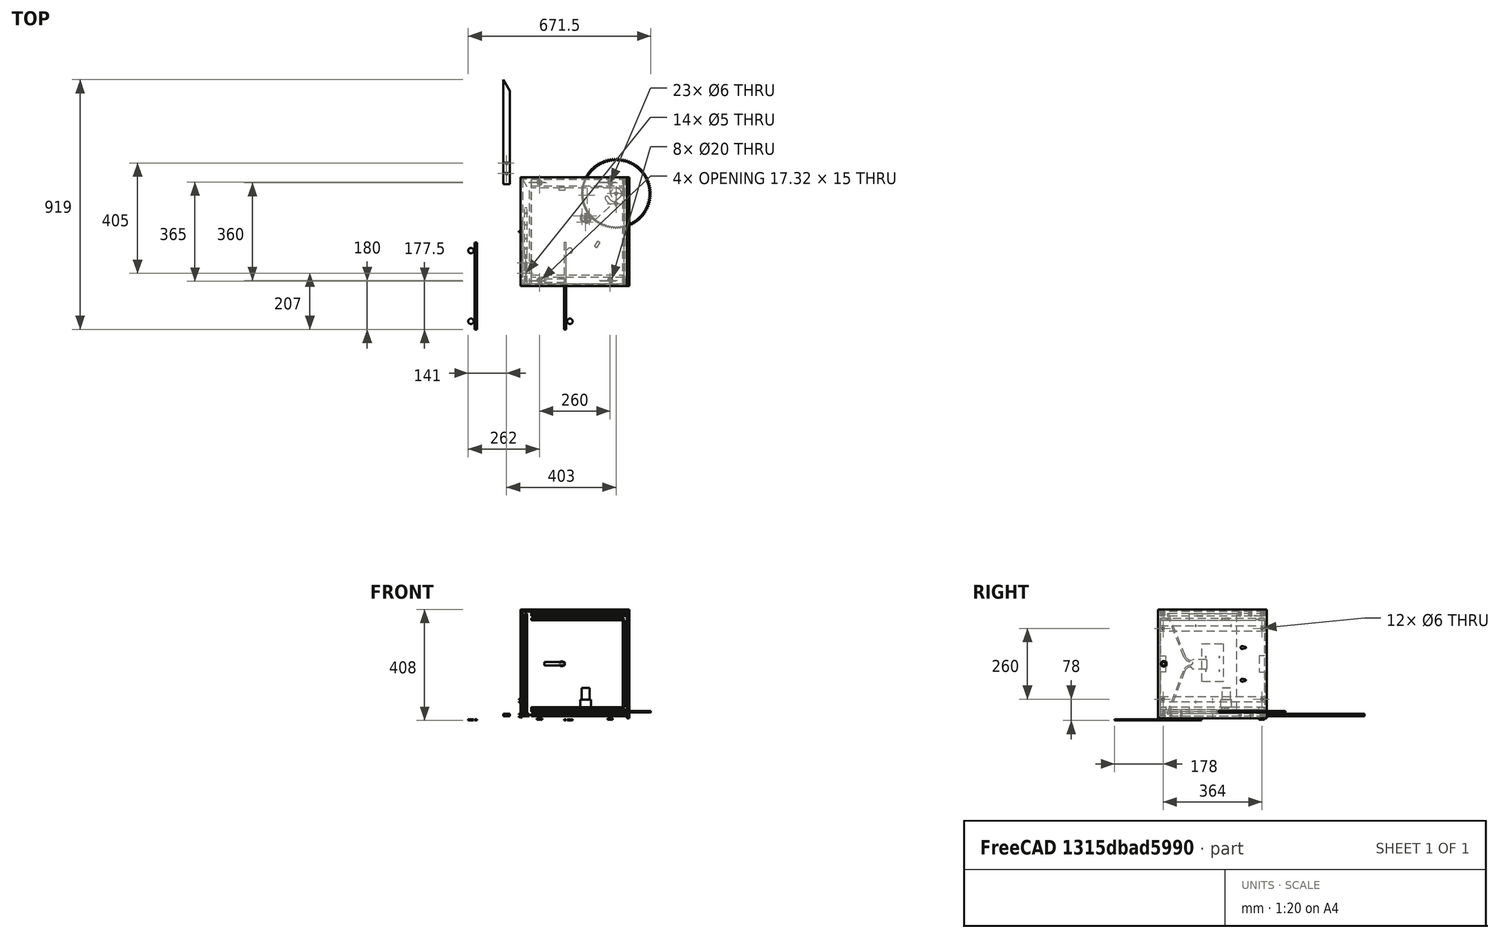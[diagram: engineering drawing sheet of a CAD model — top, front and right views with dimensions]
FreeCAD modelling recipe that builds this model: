
FCSTD DOCUMENT  (FreeCAD 0.16R6707 (Git))
Label: Latskap
License: All rights reserved
LicenseURL: http://en.wikipedia.org/wiki/All_rights_reserved
objects: Sketcher::SketchObject×47, Part::Part2DObjectPython×33, PartDesign::Pad×29, PartDesign::Pocket×18, Part::FeaturePython×9, Part::Feature×7, Part::Mirroring×6, PartDesign::Draft×5, App::DocumentObjectGroup×5, PartDesign::LinearPattern×2, Spreadsheet::Sheet×2, PartDesign::Revolution×1, PartDesign::Mirrored×1, PartDesign::MultiTransform×1, Mesh::Feature×1
note: 207 computed .brp shape members not serialized (recipe doc carries the construction recipe); baked Part::Feature solids carry a one-line shape summary decoded from their .brp

FEATURE [Sketcher::SketchObject] Sketch003
  expr: Constraints[8] = Latskap.width
  expr: Constraints[10] = Latskap.height
  sketch-geometry (4):
    g0: LineSegment StartX=0 StartY=-200 StartZ=0 EndX=400 EndY=-200 EndZ=0
    g1: LineSegment StartX=400 StartY=-200 StartZ=0 EndX=400 EndY=200 EndZ=0
    g2: LineSegment StartX=400 StartY=200 StartZ=0 EndX=0 EndY=200 EndZ=0
    g3: LineSegment StartX=0 StartY=200 StartZ=0 EndX=0 EndY=-200 EndZ=0
  constraints (12):
    c: Coincident(g0,g1)
    c: Coincident(g1,g2)
    c: Coincident(g2,g3)
    c: Coincident(g3,g0)
    c: Horizontal(g0)
    c: Horizontal(g2)
    c: Vertical(g1)
    c: Vertical(g3)
    c: DistanceX(g2,g2) = 400
    c: PointOnObject(g2,g-2)
    c: DistanceY(g1,g1) = 400
    c: Symmetric(g1,g0,g-1)
FEATURE [PartDesign::Pad] Pad002  label="Wall-outer"
  Length = 8
  Length2 = 100
  Sketch = -> Sketch003
  Type = 0
FEATURE [Sketcher::SketchObject] Sketch006
  Placement = pos=(0,0,8) rot=(0,0,1;0rad)
  expr: Constraints[36] = (Latskap.width - Latskap.bolt_distance) / 2
  expr: Constraints[11] = Latskap.arm_offset
  expr: Constraints[16] = Latskap.arm_offset
  expr: Constraints[35] = Latskap.bolt_offset
  expr: Constraints[32] = Latskap.bolt_distance
  expr: Constraints[6] = Latskap.wall_inner
  sketch-geometry (14):
    g0: LineSegment StartX=40 StartY=192 StartZ=0 EndX=392 EndY=192 EndZ=0
    g1: LineSegment StartX=392 StartY=192 StartZ=0 EndX=392 EndY=-192 EndZ=0
    g2: LineSegment StartX=392 StartY=-192 StartZ=0 EndX=40 EndY=-192 EndZ=0
    g3: LineSegment StartX=40 StartY=192 StartZ=0 EndX=40 EndY=-192 EndZ=0
    g4: Circle CenterX=352 CenterY=102 CenterZ=0 NormalX=0 NormalY=0 NormalZ=1 Radius=2.5
    g5: Circle CenterX=352 CenterY=140 CenterZ=0 NormalX=0 NormalY=0 NormalZ=1 Radius=2.5
    g6: Circle CenterX=70 CenterY=180 CenterZ=0 NormalX=0 NormalY=0 NormalZ=1 Radius=3
    g7: Circle CenterX=330 CenterY=180 CenterZ=0 NormalX=0 NormalY=0 NormalZ=1 Radius=3
    g8: Circle CenterX=70 CenterY=-179.546 CenterZ=0 NormalX=0 NormalY=0 NormalZ=1 Radius=3
    g9: Circle CenterX=330 CenterY=-179.546 CenterZ=0 NormalX=0 NormalY=0 NormalZ=1 Radius=3
    g10: LineSegment [constr] StartX=70 StartY=180 StartZ=0 EndX=330 EndY=180 EndZ=0
    g11: LineSegment [constr] StartX=330 StartY=180 StartZ=0 EndX=330 EndY=-179.546 EndZ=0
    g12: LineSegment [constr] StartX=330 StartY=-179.546 StartZ=0 EndX=70 EndY=-179.546 EndZ=0
    g13: LineSegment [constr] StartX=70 StartY=-179.546 StartZ=0 EndX=70 EndY=180 EndZ=0
  constraints (37):
    c: Coincident(g0,g1)
    c: Coincident(g1,g2)
    c: Horizontal(g0)
    c: Horizontal(g2)
    c: Vertical(g1)
    c: DistanceX(g0,g0) = 352
    c: DistanceY(g1,g1) = 384
    c: Symmetric(g0,g2,g-1)
    c: Vertical(g3)
    c: Coincident(g2,g3)
    c: Radius(g4) = 2.5
    c: DistanceX(g4) = 352
    c: DistanceY(g4) = 102
    c: DistanceX(g0) = 40
    c: Coincident(g0,g3)
    c: Radius(g5) = 2.5
    c: DistanceX(g5) = 352
    c: DistanceY(g4,g5) = 38
    c: Equal(g6,g7)
    c: Equal(g7,g8)
    c: Equal(g8,g9)
    c: Radius(g9) = 3
    c: Coincident(g10,g11)
    c: Coincident(g11,g12)
    c: Coincident(g12,g13)
    c: Coincident(g13,g10)
    c: Horizontal(g10)
    c: Horizontal(g12)
    c: Vertical(g11)
    c: Vertical(g13)
    c: Coincident(g9,g11)
    c: Coincident(g8,g12)
    c: DistanceX(g12,g12) = 260
    c: Coincident(g10,g7)
    c: Coincident(g6,g10)
    c: DistanceY(g7) = 180
    c: DistanceX(g6) = 70
FEATURE [PartDesign::Pad] Pad004  label="Wall-1-1"
  Length = 8
  Length2 = 100
  Placement = pos=(0,0,8) rot=(0,0,1;0rad)
  Sketch = -> Sketch006
  Type = 0
FEATURE [Sketcher::SketchObject] Sketch012
  expr: Constraints[9] = Latskap.height
  sketch-geometry (4):
    g0: LineSegment StartX=8 StartY=-200 StartZ=0 EndX=0 EndY=-200 EndZ=0
    g1: LineSegment StartX=0 StartY=-200 StartZ=0 EndX=0 EndY=200 EndZ=0
    g2: LineSegment StartX=0 StartY=200 StartZ=0 EndX=8 EndY=200 EndZ=0
    g3: LineSegment StartX=8 StartY=200 StartZ=0 EndX=8 EndY=-200 EndZ=0
  constraints (12):
    c: Coincident(g0,g1)
    c: Coincident(g1,g2)
    c: Coincident(g2,g3)
    c: Coincident(g3,g0)
    c: Horizontal(g0)
    c: Horizontal(g2)
    c: Vertical(g1)
    c: Vertical(g3)
    c: DistanceX(g2,g2) = 8
    c: DistanceY(g1,g1) = 400
    c: Symmetric(g1,g0,g-1)
    c: DistanceX(g1) = 0
FEATURE [PartDesign::Pad] Pad008  label="Door-outer"
  Length = 400
  Length2 = 100
  Sketch = -> Sketch012
  Type = 0
FEATURE [Sketcher::SketchObject] Sketch014
  Placement = pos=(0,0,16) rot=(0,0,1;0rad)
  sketch-geometry (11):
    g0: LineSegment StartX=20 StartY=-163 StartZ=0 EndX=186.401 EndY=-163 EndZ=0
    g1: LineSegment StartX=194.788 StartY=-158.446 StartZ=0 EndX=360.387 EndY=96.5536 EndZ=0
    g2: LineSegment StartX=343.613 StartY=107.446 StartZ=0 EndX=183.929 EndY=-138.446 EndZ=0
    g3: LineSegment StartX=175.542 StartY=-143 StartZ=0 EndX=20 EndY=-143 EndZ=0
    g4: ArcOfCircle CenterX=20 CenterY=-153 CenterZ=0 NormalX=0 NormalY=0 NormalZ=1 Radius=10 StartAngle=1.57079 EndAngle=4.71239
    g5: ArcOfCircle CenterX=186.401 CenterY=-153 CenterZ=0 NormalX=0 NormalY=0 NormalZ=1 Radius=10 StartAngle=4.71239 EndAngle=5.70723
    g6: ArcOfCircle CenterX=175.542 CenterY=-133 CenterZ=0 NormalX=0 NormalY=0 NormalZ=1 Radius=10 StartAngle=4.71239 EndAngle=5.70723
    g7: ArcOfCircle CenterX=352 CenterY=102 CenterZ=0 NormalX=0 NormalY=0 NormalZ=1 Radius=10 StartAngle=5.70723 EndAngle=8.84882
    g8: Circle CenterX=20 CenterY=-153 CenterZ=0 NormalX=0 NormalY=0 NormalZ=1 Radius=5
    g9: Circle CenterX=352 CenterY=102 CenterZ=0 NormalX=0 NormalY=0 NormalZ=1 Radius=5
    g10: LineSegment [constr] StartX=213.605 StartY=-92.7491 StartZ=0 EndX=230.378 EndY=-103.642 EndZ=0
  constraints (30):
    c: Coincident(g3,g4)
    c: Coincident(g0,g4)
    c: Tangent(g0,g5) = -1.5708
    c: Tangent(g1,g5) = -1.5708
    c: Tangent(g3,g6) = 1.5708
    c: Tangent(g2,g6) = 1.5708
    c: Coincident(g7,g1)
    c: Coincident(g7,g2)
    c: Tangent(g2,g7)
    c: Tangent(g7,g1)
    c: Tangent(g4,g3)
    c: Tangent(g4,g0)
    c: Horizontal(g3)
    c: Horizontal(g0)
    c: Equal(g5,g6)
    c: Equal(g6,g4)
    c: Equal(g4,g7)
    c: Radius(g8) = 5
    c: Radius(g4) = 10
    c: Coincident(g8,g4)
    c: Coincident(g7,g9)
    c: Radius(g9) = 5
    c: DistanceX(g4) = 20
    c: DistanceX(g7) = 352
    c: DistanceY(g7) = 102
    c: DistanceY(g4,g7) = 255
    c: Perpendicular(g10,g2) = 4.71239
    c: Angle(g1) = 0.994838
    c: Distance(g10) = 20
    c: PointOnObject(g10,g1)
FEATURE [PartDesign::Pad] Pad009  label="arm-lower"
  Length = 6
  Length2 = 100
  Placement = pos=(0,0,16) rot=(0,0,1;0rad)
  Sketch = -> Sketch014
  Type = 0
FEATURE [Sketcher::SketchObject] Sketch015
  Placement = pos=(0,0,16) rot=(0,0,1;0rad)
  expr: Constraints[10] = Latskap.arm_offset
  sketch-geometry (13):
    g0: LineSegment StartX=20 StartY=-125 StartZ=0 EndX=186.401 EndY=-125 EndZ=0
    g1: LineSegment StartX=170.857 StartY=-105 StartZ=0 EndX=20 EndY=-105 EndZ=0
    g2: ArcOfCircle CenterX=20 CenterY=-115 CenterZ=0 NormalX=0 NormalY=0 NormalZ=1 Radius=10 StartAngle=1.5708 EndAngle=4.71239
    g3: ArcOfCircle CenterX=352 CenterY=140 CenterZ=0 NormalX=0 NormalY=0 NormalZ=1 Radius=10 StartAngle=5.70723 EndAngle=8.84882
    g4: ArcOfCircle CenterX=186.401 CenterY=-115 CenterZ=0 NormalX=0 NormalY=0 NormalZ=1 Radius=10 StartAngle=4.71239 EndAngle=5.70723
    g5: Circle CenterX=20 CenterY=-115 CenterZ=0 NormalX=0 NormalY=0 NormalZ=1 Radius=5
    g6: LineSegment StartX=343.613 StartY=145.446 StartZ=0 EndX=186.48 EndY=-96.5174 EndZ=0
    g7: LineSegment StartX=360.387 StartY=134.554 StartZ=0 EndX=194.788 EndY=-120.446 EndZ=0
    g8: ArcOfCircle CenterX=170.857 CenterY=-86.3717 CenterZ=0 NormalX=0 NormalY=0 NormalZ=1 Radius=18.6283 StartAngle=4.71239 EndAngle=5.70723
    g9: LineSegment [constr] StartX=203.417 StartY=-70.4363 StartZ=0 EndX=220.191 EndY=-81.3291 EndZ=0
    g10: Circle CenterX=352 CenterY=140 CenterZ=0 NormalX=0 NormalY=0 NormalZ=1 Radius=5
    g11: LineSegment [constr] StartX=352 StartY=140 StartZ=0 EndX=292.726 EndY=52.122 EndZ=0
    g12: Circle CenterX=292.726 CenterY=52.122 CenterZ=0 NormalX=0 NormalY=0 NormalZ=1 Radius=1.3
  constraints (36):
    c: Tangent(g0,g4) = -1.5708
    c: Coincident(g1,g2)
    c: Coincident(g0,g2)
    c: Tangent(g2,g1)
    c: Tangent(g2,g0)
    c: Equal(g4,g3)
    c: Radius(g3) = 10
    c: Coincident(g2,g5)
    c: Radius(g5) = 5
    c: DistanceX(g2) = 20
    c: DistanceX(g3) = 352
    c: DistanceY(g3) = 140
    c: DistanceY(g2,g3) = 255
    c: Radius(g2) = 10
    c: Tangent(g1,g8) = 1.5708
    c: Tangent(g6,g8) = 1.5708
    c: Coincident(g4,g7)
    c: Perpendicular(g6,g9)
    c: PointOnObject(g9,g6)
    c: PointOnObject(g9,g7)
    c: Distance(g9) = 20
    c: Coincident(g3,g7)
    c: Coincident(g3,g6)
    c: Tangent(g7,g3)
    c: Tangent(g6,g3)
    c: Tangent(g4,g7)
    c: Angle(g7) = -2.14675
    c: Radius(g10) = 5
    c: Coincident(g10,g3)
    c: Distance(g11) = 106
    c: Coincident(g11,g3)
    c: Radius(g12) = 1.3
    c: Coincident(g12,g11)
    c: Angle(g11) = -2.16421
    c: Horizontal(g1)
    c: Horizontal(g0)
FEATURE [PartDesign::Pad] Pad010  label="Arm-upper"
  Length = 6
  Length2 = 100
  Placement = pos=(0,0,16) rot=(0,0,1;0rad)
  Sketch = -> Sketch015
  Type = 0
FEATURE [Sketcher::SketchObject] Sketch016
  Placement = pos=(400,0,0) rot=(0.57735,0.57735,0.57735;2.0944rad)
  expr: Constraints[30] = 8 + 10
  sketch-geometry (30):
    g0: LineSegment StartX=-200 StartY=0 StartZ=0 EndX=200 EndY=0 EndZ=0
    g1: LineSegment StartX=200 StartY=0 StartZ=0 EndX=200 EndY=400 EndZ=0
    g2: LineSegment StartX=200 StartY=400 StartZ=0 EndX=-200 EndY=400 EndZ=0
    g3: LineSegment StartX=-200 StartY=400 StartZ=0 EndX=-200 EndY=0 EndZ=0
    g4: LineSegment [constr] StartX=-182 StartY=330 StartZ=0 EndX=182 EndY=330 EndZ=0
    g5: LineSegment [constr] StartX=182 StartY=330 StartZ=0 EndX=182 EndY=70 EndZ=0
    g6: LineSegment [constr] StartX=182 StartY=70 StartZ=0 EndX=-182 EndY=70 EndZ=0
    g7: LineSegment [constr] StartX=-182 StartY=70 StartZ=0 EndX=-182 EndY=330 EndZ=0
    g8: Circle CenterX=-182 CenterY=330 CenterZ=0 NormalX=0 NormalY=0 NormalZ=1 Radius=3
    g9: Circle CenterX=182 CenterY=330 CenterZ=0 NormalX=0 NormalY=0 NormalZ=1 Radius=3
    g10: Circle CenterX=182 CenterY=70 CenterZ=0 NormalX=0 NormalY=0 NormalZ=1 Radius=3
    g11: Circle CenterX=-182 CenterY=70 CenterZ=0 NormalX=0 NormalY=0 NormalZ=1 Radius=3
    g12: LineSegment [constr] StartX=-200 StartY=200 StartZ=0 EndX=200 EndY=200 EndZ=0
    g13: ArcOfCircle CenterX=120 CenterY=260 CenterZ=0 NormalX=0 NormalY=0 NormalZ=1 Radius=2.7 StartAngle=4.71238 EndAngle=7.85399
    g14: LineSegment StartX=120 StartY=257.3 StartZ=0 EndX=115 EndY=257.3 EndZ=0
    g15: LineSegment StartX=120 StartY=262.7 StartZ=0 EndX=115 EndY=262.7 EndZ=0
    g16: LineSegment StartX=115 StartY=262.7 StartZ=0 EndX=113.39 EndY=265 EndZ=0
    g17: LineSegment StartX=113.39 StartY=265 StartZ=0 EndX=108.39 EndY=265 EndZ=0
    g18: LineSegment StartX=115 StartY=257.3 StartZ=0 EndX=113.39 EndY=255 EndZ=0
    g19: LineSegment StartX=113.39 StartY=255 StartZ=0 EndX=108.39 EndY=255 EndZ=0
    g20: ArcOfCircle CenterX=108.39 CenterY=260 CenterZ=0 NormalX=0 NormalY=0 NormalZ=1 Radius=5 StartAngle=1.5708 EndAngle=4.71239
    g21: ArcOfCircle CenterX=120 CenterY=140 CenterZ=0 NormalX=0 NormalY=0 NormalZ=1 Radius=2.7 StartAngle=4.71239 EndAngle=7.85398
    g22: LineSegment StartX=120 StartY=142.7 StartZ=0 EndX=115 EndY=142.7 EndZ=0
    g23: LineSegment StartX=115 StartY=142.7 StartZ=0 EndX=113.39 EndY=145 EndZ=0
    g24: LineSegment StartX=113.39 StartY=145 StartZ=0 EndX=108.39 EndY=145 EndZ=0
    g25: LineSegment StartX=120 StartY=137.3 StartZ=0 EndX=115 EndY=137.3 EndZ=0
    g26: LineSegment StartX=113.39 StartY=135 StartZ=0 EndX=115 EndY=137.3 EndZ=0
    g27: LineSegment StartX=113.39 StartY=135 StartZ=0 EndX=108.39 EndY=135 EndZ=0
    g28: ArcOfCircle CenterX=108.39 CenterY=140 CenterZ=0 NormalX=0 NormalY=0 NormalZ=1 Radius=5 StartAngle=1.5708 EndAngle=4.71239
    g29: Circle CenterX=-180 CenterY=200 CenterZ=0 NormalX=0 NormalY=0 NormalZ=1 Radius=10
  constraints (91):
    c: Coincident(g0,g1)
    c: Coincident(g1,g2)
    c: Coincident(g2,g3)
    c: Coincident(g3,g0)
    c: Horizontal(g0)
    c: Horizontal(g2)
    c: Vertical(g1)
    c: Vertical(g3)
    c: DistanceY(g1,g1) = 400
    c: DistanceX(g2,g2) = 400
    c: PointOnObject(g0,g-1)
    c: Symmetric(g0,g0,g-2)
    c: Coincident(g4,g5)
    c: Coincident(g5,g6)
    c: Coincident(g6,g7)
    c: Coincident(g7,g4)
    c: Horizontal(g4)
    c: Horizontal(g6)
    c: Vertical(g5)
    c: Vertical(g7)
    c: Symmetric(g4,g4,g-2)
    c: DistanceY(g5,g5) = 260
    c: Coincident(g6,g11)
    c: Coincident(g8,g4)
    c: Coincident(g4,g9)
    c: Coincident(g10,g5)
    c: Equal(g9,g8)
    c: Equal(g8,g11)
    c: Equal(g11,g10)
    c: Radius(g9) = 3
    c: DistanceX(g0,g6) = 18
    c: Horizontal(g12)
    c: PointOnObject(g12,g3)
    c: PointOnObject(g12,g1)
    c: DistanceY(g0,g12) = 200
    c: Symmetric(g4,g5,g12)
    c: Coincident(g19,g20)
    c: Coincident(g17,g20)
    c: Coincident(g16,g17)
    c: Coincident(g15,g16)
    c: Radius(g13) = 2.7
    c: Coincident(g13,g15)
    c: Radius(g20) = 5
    c: Tangent(g20,g17)
    c: Tangent(g20,g19)
    c: Coincident(g18,g19)
    c: Coincident(g14,g18)
    c: Coincident(g13,g14)
    c: Tangent(g14,g13)
    c: Tangent(g15,g13)
    c: Horizontal(g17)
    c: Horizontal(g19)
    c: Horizontal(g15)
    c: Horizontal(g14)
    c: Equal(g18,g16)
    c: Angle(g18,g19) = 2.18166
    c: Equal(g15,g14)
    c: Angle(g17,g16) = 2.18166
    c: DistanceX(g13,g1) = 80
    c: DistanceY(g12,g13) = 60
    c: DistanceX(g17,g17) = 5
    c: DistanceX(g15,g15) = 5
    c: Coincident(g27,g28)
    c: Coincident(g26,g27)
    c: Coincident(g25,g26)
    c: Equal(g25,g22)
    c: Coincident(g23,g24)
    c: Coincident(g22,g23)
    c: Coincident(g24,g28)
    c: Coincident(g21,g22)
    c: Coincident(g21,g25)
    c: Radius(g21) = 2.7
    c: Horizontal(g22)
    c: Horizontal(g25)
    c: Horizontal(g24)
    c: Horizontal(g27)
    c: Angle(g24,g23) = 2.18166
    c: Angle(g26,g27) = 2.18166
    c: Tangent(g25,g21)
    c: Tangent(g22,g21)
    c: Tangent(g28,g24)
    c: Tangent(g28,g27)
    c: DistanceX(g22,g22) = 5
    c: DistanceX(g21,g12) = 80
    c: Equal(g26,g23)
    c: Equal(g24,g22)
    c: DistanceY(g12,g21) = -60
    c: Radius(g28) = 5
    c: PointOnObject(g29,g12)
    c: Radius(g29) = 10
    c: DistanceX(g12,g29) = 20
FEATURE [PartDesign::Pad] Pad011  label="Back-straight"
  Length = 8
  Length2 = 100
  Placement = pos=(400,0,0) rot=(0.57735,0.57735,0.57735;2.0944rad)
  Reversed = true
  Sketch = -> Sketch016
  Type = 0
FEATURE [Part::Part2DObjectPython] Clone2D  label="Clone of Sketch015 (2D)"  # Draft 2D object (typed FeaturePython)
  Objects = -> [Sketch015]
  Placement = pos=(28.3521,336.866,16) rot=(0,0,-1;0.925025rad)
  Scale = (1,1,1)
FEATURE [Part::Part2DObjectPython] Clone2D001  label="Clone of Sketch014 (2D)"  # Draft 2D object (typed FeaturePython)
  Objects = -> [Sketch014]
  Placement = pos=(58.7003,321.735,16) rot=(0,0,-1;0.925025rad)
  Scale = (1,1,1)
FEATURE [Sketcher::SketchObject] Sketch
  Placement = pos=(0,0,32) rot=(0,0,1;0rad)
  expr: Constraints[57] = Latskap.arm_upper
  expr: Constraints[56] = Latskap.arm_offset
  expr: Constraints[40] = Latskap.bolt_offset
  expr: Constraints[42] = Latskap.bolt_pos
  expr: Constraints[30] = Latskap.motor_x
  expr: Constraints[39] = Latskap.bolt_distance
  expr: Constraints[25] = Latskap.motor_y
  sketch-geometry (23):
    g0: Circle CenterX=246.8 CenterY=50.5 CenterZ=0 NormalX=0 NormalY=0 NormalZ=1 Radius=6.5
    g1: Circle CenterX=239.8 CenterY=35 CenterZ=0 NormalX=0 NormalY=0 NormalZ=1 Radius=3
    g2: Circle CenterX=226.377 CenterY=58.25 CenterZ=0 NormalX=0 NormalY=0 NormalZ=1 Radius=3
    g3: Circle CenterX=253.223 CenterY=58.25 CenterZ=0 NormalX=0 NormalY=0 NormalZ=1 Radius=3
    g4: Circle [constr] CenterX=239.8 CenterY=50.5 CenterZ=0 NormalX=0 NormalY=0 NormalZ=1 Radius=15.5
    g5: LineSegment [constr] StartX=239.8 StartY=35 StartZ=0 EndX=239.8 EndY=50.5 EndZ=0
    g6: LineSegment [constr] StartX=239.8 StartY=50.5 StartZ=0 EndX=253.223 EndY=58.25 EndZ=0
    g7: LineSegment [constr] StartX=226.377 StartY=58.25 StartZ=0 EndX=239.8 EndY=50.5 EndZ=0
    g8: LineSegment StartX=40 StartY=192 StartZ=0 EndX=392 EndY=192 EndZ=0
    g9: LineSegment StartX=392 StartY=192 StartZ=0 EndX=392 EndY=-182 EndZ=0
    g10: LineSegment StartX=382 StartY=-192 StartZ=0 EndX=40 EndY=-192 EndZ=0
    g11: LineSegment StartX=40 StartY=-192 StartZ=0 EndX=40 EndY=192 EndZ=0
    g12: LineSegment [constr] StartX=70 StartY=180 StartZ=0 EndX=330 EndY=180 EndZ=0
    g13: LineSegment [constr] StartX=330 StartY=180 StartZ=0 EndX=330 EndY=-180 EndZ=0
    g14: LineSegment [constr] StartX=330 StartY=-180 StartZ=0 EndX=70 EndY=-180 EndZ=0
    g15: LineSegment [constr] StartX=70 StartY=-180 StartZ=0 EndX=70 EndY=180 EndZ=0
    g16: Circle CenterX=70 CenterY=180 CenterZ=0 NormalX=0 NormalY=0 NormalZ=1 Radius=3
    g17: Circle CenterX=330 CenterY=180 CenterZ=0 NormalX=0 NormalY=0 NormalZ=1 Radius=3
    g18: Circle CenterX=70 CenterY=-180 CenterZ=0 NormalX=0 NormalY=0 NormalZ=1 Radius=3
    g19: Circle CenterX=330 CenterY=-180 CenterZ=0 NormalX=0 NormalY=0 NormalZ=1 Radius=3
    g20: LineSegment StartX=382 StartY=-192 StartZ=0 EndX=382 EndY=-182 EndZ=0
    g21: LineSegment StartX=382 StartY=-182 StartZ=0 EndX=392 EndY=-182 EndZ=0
    g22: Circle CenterX=352 CenterY=140 CenterZ=0 NormalX=0 NormalY=0 NormalZ=1 Radius=20
  constraints (58):
    c: Radius(g0) = 6.5
    c: Equal(g3,g1)
    c: Equal(g1,g2)
    c: Radius(g1) = 3
    c: Radius(g4) = 15.5
    c: PointOnObject(g2,g4)
    c: PointOnObject(g3,g4)
    c: PointOnObject(g1,g4)
    c: DistanceX(g4,g0) = 7
    c: DistanceY(g0,g4) = 0
    c: Angle(g5,g6) = 2.0944
    c: Coincident(g4,g5)
    c: Coincident(g4,g6)
    c: Coincident(g6,g3)
    c: Coincident(g5,g1)
    c: Coincident(g2,g7)
    c: Coincident(g7,g4)
    c: Angle(g7,g5) = 2.0944
    c: Coincident(g8,g9)
    c: Coincident(g10,g11)
    c: Coincident(g11,g8)
    c: Horizontal(g8)
    c: Horizontal(g10)
    c: Vertical(g9)
    c: Vertical(g11)
    c: DistanceY(g0) = 50.5
    c: DistanceX(g8) = 40
    c: DistanceY(g11,g11) = 384
    c: Symmetric(g8,g10,g-1)
    c: DistanceX(g8,g8) = 352
    c: DistanceX(g0) = 246.8
    c: Coincident(g12,g13)
    c: Coincident(g13,g14)
    c: Coincident(g14,g15)
    c: Coincident(g15,g12)
    c: Horizontal(g12)
    c: Horizontal(g14)
    c: Vertical(g13)
    c: Vertical(g15)
    c: DistanceX(g12,g12) = 260
    c: DistanceY(g12) = 180
    c: Symmetric(g12,g13,g-1)
    c: DistanceX(g12) = 70
    c: Equal(g19,g18)
    c: Equal(g18,g16)
    c: Equal(g16,g17)
    c: Radius(g17) = 3
    c: Coincident(g20,g21)
    c: Coincident(g9,g21)
    c: Horizontal(g21)
    c: Vertical(g20)
    c: Coincident(g10,g20)
    c: DistanceX(g21,g21) = 10
    c: DistanceY(g20,g20) = 10
    c: Vertical(g5)
    c: Radius(g22) = 20
    c: DistanceX(g22) = 352
    c: DistanceY(g22) = 140
FEATURE [Sketcher::SketchObject] Sketch019
  Placement = pos=(0,0,8) rot=(0,0,1;0rad)
  sketch-geometry (6):
    g0: LineSegment StartX=8 StartY=192 StartZ=0 EndX=32 EndY=150.431 EndZ=0
    g1: LineSegment StartX=32 StartY=150.431 StartZ=0 EndX=32 EndY=-192 EndZ=0
    g2: LineSegment StartX=32 StartY=-192 StartZ=0 EndX=8 EndY=-192 EndZ=0
    g3: LineSegment StartX=8 StartY=-192 StartZ=0 EndX=8 EndY=192 EndZ=0
    g4: Circle CenterX=20 CenterY=-115 CenterZ=0 NormalX=0 NormalY=0 NormalZ=1 Radius=2.5
    g5: Circle CenterX=20 CenterY=-153 CenterZ=0 NormalX=0 NormalY=0 NormalZ=1 Radius=2.5
  constraints (18):
    c: Coincident(g0,g1)
    c: Coincident(g1,g2)
    c: Coincident(g2,g3)
    c: Coincident(g3,g0)
    c: Horizontal(g2)
    c: Vertical(g1)
    c: Vertical(g3)
    c: DistanceX(g2,g2) = 24
    c: DistanceY(g5,g4) = 38
    c: DistanceX(g5) = 20
    c: DistanceX(g4) = 20
    c: DistanceY(g4) = -115
    c: Radius(g5) = 2.5
    c: Radius(g4) = 2.5
    c: Symmetric(g2,g0,g-1)
    c: DistanceX(g1) = 32
    c: DistanceY(g3,g3) = 384
    c: Angle(g3,g0) = 0.523599
FEATURE [PartDesign::Pad] Pad013  label="Door-side-1-1"
  Length = 8
  Length2 = 100
  Placement = pos=(0,0,8) rot=(0,0,1;0rad)
  Sketch = -> Sketch019
  Type = 0
FEATURE [PartDesign::Pad] Pad014  label="Wall-3-1"
  Length = 8
  Length2 = 100
  Placement = pos=(0,0,32) rot=(0,0,1;0rad)
  Reversed = true
  Sketch = -> Sketch
  Type = 0
FEATURE [Sketcher::SketchObject] Sketch021
  ExternalGeometry = -> [Pad013]
  Placement = pos=(0,0,8) rot=(1,0,0;3.14159rad)
  Support = -> Pad013 [Face7]
  sketch-geometry (6):
    g0: LineSegment [constr] StartX=20 StartY=115 StartZ=0 EndX=20 EndY=123 EndZ=0
    g1: LineSegment [constr] StartX=20 StartY=115 StartZ=0 EndX=13.0718 EndY=111 EndZ=0
    g2: LineSegment [constr] StartX=20 StartY=115 StartZ=0 EndX=26.9282 EndY=111 EndZ=0
    g3: LineSegment StartX=20 StartY=123 StartZ=0 EndX=13.0718 EndY=111 EndZ=0
    g4: LineSegment StartX=26.9282 StartY=111 StartZ=0 EndX=13.0718 EndY=111 EndZ=0
    g5: LineSegment StartX=26.9282 StartY=111 StartZ=0 EndX=20 EndY=123 EndZ=0
  constraints (15):
    c: Coincident(g0,g1)
    c: Coincident(g0,g2)
    c: Coincident(g0,g-3)
    c: Coincident(g0,g3)
    c: Coincident(g0,g5)
    c: Coincident(g1,g3)
    c: Coincident(g1,g4)
    c: Coincident(g2,g4)
    c: Coincident(g2,g5)
    c: Equal(g2,g1)
    c: Equal(g1,g0)
    c: Equal(g5,g3)
    c: Equal(g3,g4)
    c: Horizontal(g4)
    c: DistanceY(g2,g0) = 4
FEATURE [PartDesign::Pocket] Pocket  label="Door-1-2"
  Length = 4.5
  Placement = pos=(0,0,8) rot=(0,0,1;0rad)
  Sketch = -> Sketch021
  Type = 0
FEATURE [PartDesign::LinearPattern] LinearPattern001  label="Door-side-1"
  Direction = -> Sketch021 [V_Axis]
  Length = 38
  Occurrences = 2
  Originals = -> [Pocket]
  Placement = pos=(0,0,8) rot=(0,0,1;0rad)
FEATURE [Sketcher::SketchObject] Sketch022
  Placement = pos=(239.8,50.5,40) rot=(1,0,0;1.5708rad)
  expr: Placement.Base.y = Latskap.motor_y
  expr: Placement.Base.x = Latskap.motor_x - 7
  sketch-geometry (6):
    g0: LineSegment StartX=-20 StartY=0 StartZ=0 EndX=-20 EndY=29 EndZ=0
    g1: LineSegment StartX=-20 StartY=29 StartZ=0 EndX=-15 EndY=29 EndZ=0
    g2: LineSegment StartX=-15 StartY=29 StartZ=0 EndX=-15 EndY=71 EndZ=0
    g3: LineSegment StartX=-15 StartY=71 StartZ=0 EndX=0 EndY=71 EndZ=0
    g4: LineSegment StartX=-20 StartY=0 StartZ=0 EndX=0 EndY=0 EndZ=0
    g5: LineSegment StartX=0 StartY=0 StartZ=0 EndX=0 EndY=71 EndZ=0
  constraints (18):
    c: Coincident(g0,g1)
    c: Coincident(g1,g2)
    c: Coincident(g2,g3)
    c: PointOnObject(g3,g-2)
    c: Coincident(g4,g5)
    c: Coincident(g3,g5)
    c: Coincident(g4,g-1)
    c: PointOnObject(g0,g-1)
    c: PointOnObject(g4,g-1)
    c: Horizontal(g1)
    c: Vertical(g0)
    c: Vertical(g2)
    c: Horizontal(g3)
    c: DistanceX(g2) = -15
    c: DistanceX(g0) = -20
    c: Coincident(g4,g0)
    c: DistanceY(g0,g0) = 29
    c: DistanceY(g2,g2) = 42
FEATURE [PartDesign::Revolution] Revolution  label="Motor-no-shaft"
  Angle = 360
  Axis = (0,0,1)
  Base = (239.8,50.5,40)
  Placement = pos=(239.8,50.5,40) rot=(1,0,0;1.5708rad)
  ReferenceAxis = -> Sketch022 [V_Axis]
  Sketch = -> Sketch022
FEATURE [Sketcher::SketchObject] Sketch023
  Placement = pos=(0,0,40) rot=(0,0,1;0rad)
  expr: Constraints[44] = Latskap001.bolt_pos
  expr: Constraints[10] = Latskap001.motor_y
  expr: Constraints[45] = Latskap001.bolt_offset
  expr: Constraints[42] = Latskap001.bolt_distance
  expr: Constraints[9] = Latskap001.motor_x - 7
  sketch-geometry (21):
    g0: LineSegment StartX=40 StartY=192 StartZ=0 EndX=380 EndY=192 EndZ=0
    g1: LineSegment StartX=380 StartY=192 StartZ=0 EndX=380 EndY=-192 EndZ=0
    g2: LineSegment StartX=380 StartY=-192 StartZ=0 EndX=40 EndY=-192 EndZ=0
    g3: LineSegment StartX=40 StartY=-192 StartZ=0 EndX=40 EndY=192 EndZ=0
    g4: Circle [constr] CenterX=239.8 CenterY=50.5 CenterZ=0 NormalX=0 NormalY=0 NormalZ=1 Radius=15.5
    g5: Circle CenterX=226.377 CenterY=58.25 CenterZ=0 NormalX=0 NormalY=0 NormalZ=1 Radius=1.7
    g6: Circle CenterX=253.223 CenterY=58.25 CenterZ=0 NormalX=0 NormalY=0 NormalZ=1 Radius=1.7
    g7: Circle CenterX=239.8 CenterY=35 CenterZ=0 NormalX=0 NormalY=0 NormalZ=1 Radius=1.7
    g8: LineSegment [constr] StartX=239.8 StartY=35 StartZ=0 EndX=239.8 EndY=50.5 EndZ=0
    g9: LineSegment [constr] StartX=226.377 StartY=58.25 StartZ=0 EndX=239.8 EndY=50.5 EndZ=0
    g10: LineSegment [constr] StartX=239.8 StartY=50.5 StartZ=0 EndX=253.223 EndY=58.25 EndZ=0
    g11: Circle CenterX=246.8 CenterY=50.5 CenterZ=0 NormalX=0 NormalY=0 NormalZ=1 Radius=6.5
    g12: LineSegment [constr] StartX=239.8 StartY=50.5 StartZ=0 EndX=246.8 EndY=50.5 EndZ=0
    g13: LineSegment [constr] StartX=70 StartY=180 StartZ=0 EndX=330 EndY=180 EndZ=0
    g14: LineSegment [constr] StartX=330 StartY=180 StartZ=0 EndX=330 EndY=-180 EndZ=0
    g15: LineSegment [constr] StartX=330 StartY=-180 StartZ=0 EndX=70 EndY=-180 EndZ=0
    g16: LineSegment [constr] StartX=70 StartY=-180 StartZ=0 EndX=70 EndY=180 EndZ=0
    g17: Circle CenterX=70 CenterY=180 CenterZ=0 NormalX=0 NormalY=0 NormalZ=1 Radius=10
    g18: Circle CenterX=330 CenterY=180 CenterZ=0 NormalX=0 NormalY=0 NormalZ=1 Radius=10
    g19: Circle CenterX=70 CenterY=-180 CenterZ=0 NormalX=0 NormalY=0 NormalZ=1 Radius=10
    g20: Circle CenterX=330 CenterY=-180 CenterZ=0 NormalX=0 NormalY=0 NormalZ=1 Radius=10
  constraints (55):
    c: Coincident(g0,g1)
    c: Coincident(g1,g2)
    c: Coincident(g2,g3)
    c: Coincident(g3,g0)
    c: Horizontal(g0)
    c: Horizontal(g2)
    c: Vertical(g1)
    c: Vertical(g3)
    c: DistanceX(g0) = 40
    c: DistanceX(g4) = 239.8
    c: DistanceY(g4) = 50.5
    c: Radius(g4) = 15.5
    c: DistanceY(g3,g3) = 384
    c: Symmetric(g2,g0,g-1)
    c: DistanceX(g0,g0) = 340
    c: PointOnObject(g5,g4)
    c: PointOnObject(g6,g4)
    c: PointOnObject(g7,g4)
    c: Coincident(g7,g8)
    c: Coincident(g5,g9)
    c: Coincident(g6,g10)
    c: Coincident(g4,g8)
    c: Coincident(g4,g9)
    c: Coincident(g4,g10)
    c: Equal(g6,g5)
    c: Equal(g5,g7)
    c: Angle(g8,g10) = 2.0944
    c: Angle(g9,g8) = 2.0944
    c: Radius(g6) = 1.7
    c: Radius(g11) = 6.5
    c: Coincident(g11,g12)
    c: Horizontal(g12)
    c: DistanceX(g4,g11) = 7
    c: Coincident(g12,g4)
    c: Coincident(g13,g14)
    c: Coincident(g14,g15)
    c: Coincident(g15,g16)
    c: Coincident(g16,g13)
    c: Horizontal(g13)
    c: Horizontal(g15)
    c: Vertical(g14)
    c: Vertical(g16)
    c: DistanceX(g15,g15) = 260
    c: Symmetric(g13,g15,g-1)
    c: DistanceX(g13) = 70
    c: DistanceY(g13) = 180
    c: Coincident(g14,g20)
    c: Coincident(g15,g19)
    c: Coincident(g13,g18)
    c: Coincident(g13,g17)
    c: Equal(g17,g18)
    c: Equal(g18,g20)
    c: Equal(g20,g19)
    c: Radius(g20) = 10
    c: Vertical(g8)
FEATURE [PartDesign::Pad] Pad015  label="Wall-inner-1"
  Length = 8
  Length2 = 100
  Placement = pos=(0,0,40) rot=(0,0,1;0rad)
  Reversed = true
  Sketch = -> Sketch023
  Type = 0
FEATURE [PartDesign::Draft] Draft  label="Wall-outer-draft"
  Angle = 45
  Base = -> Pad002 [Face1,Face4,Face3,Face2]
  NeutralPlane = -> Pad002 [Face5]
  Reversed = true
FEATURE [Sketcher::SketchObject] Sketch024
  Placement = pos=(0,0,16) rot=(0,0,1;0rad)
  expr: Constraints[31] = Latskap.bolt_distance
  expr: Constraints[3] = Latskap.wall_inner
  expr: Constraints[33] = Latskap.bolt_offset
  expr: Constraints[32] = Latskap.bolt_pos
  sketch-geometry (18):
    g0: LineSegment StartX=40 StartY=192 StartZ=0 EndX=392 EndY=192 EndZ=0
    g1: LineSegment StartX=356 StartY=-192 StartZ=0 EndX=40 EndY=-192 EndZ=0
    g2: LineSegment StartX=40 StartY=192 StartZ=0 EndX=40 EndY=168 EndZ=0
    g3: LineSegment StartX=356 StartY=-170 StartZ=0 EndX=40 EndY=-170 EndZ=0
    g4: LineSegment StartX=40 StartY=-170 StartZ=0 EndX=40 EndY=-192 EndZ=0
    g5: Circle CenterX=70 CenterY=180 CenterZ=0 NormalX=0 NormalY=0 NormalZ=1 Radius=3
    g6: Circle CenterX=330 CenterY=180 CenterZ=0 NormalX=0 NormalY=0 NormalZ=1 Radius=3
    g7: Circle CenterX=330 CenterY=-180 CenterZ=0 NormalX=0 NormalY=0 NormalZ=1 Radius=3
    g8: Circle CenterX=70 CenterY=-180 CenterZ=0 NormalX=0 NormalY=0 NormalZ=1 Radius=3
    g9: LineSegment [constr] StartX=70 StartY=180 StartZ=0 EndX=330 EndY=180 EndZ=0
    g10: LineSegment [constr] StartX=330 StartY=180 StartZ=0 EndX=330 EndY=-180 EndZ=0
    g11: LineSegment [constr] StartX=330 StartY=-180 StartZ=0 EndX=70 EndY=-180 EndZ=0
    g12: LineSegment [constr] StartX=70 StartY=-180 StartZ=0 EndX=70 EndY=180 EndZ=0
    g13: LineSegment StartX=40 StartY=168 StartZ=0 EndX=224 EndY=168 EndZ=0
    g14: ArcOfCircle CenterX=339.267 CenterY=109.195 CenterZ=0 NormalX=0 NormalY=0 NormalZ=1 Radius=129.4 StartAngle=2.53841 EndAngle=2.66985
    g15: LineSegment StartX=232.701 StartY=182.6 StartZ=0 EndX=372.907 EndY=160.096 EndZ=0
    g16: LineSegment StartX=356 StartY=-170 StartZ=0 EndX=356 EndY=-192 EndZ=0
    g17: LineSegment StartX=372.907 StartY=160.096 StartZ=0 EndX=392 EndY=192 EndZ=0
  constraints (46):
    c: Horizontal(g0)
    c: Horizontal(g1)
    c: DistanceX(g0,g0) = 352
    c: DistanceY(g1,g0) = 384
    c: Symmetric(g0,g1,g-1)
    c: DistanceX(g0) = 40
    c: Coincident(g3,g4)
    c: Vertical(g4)
    c: Horizontal(g3)
    c: Vertical(g2)
    c: DistanceY(g2,g2) = 24
    c: DistanceY(g4,g4) = 22
    c: Coincident(g1,g4)
    c: Coincident(g0,g2)
    c: Radius(g5) = 3
    c: Equal(g8,g7)
    c: Equal(g7,g6)
    c: Equal(g5,g6)
    c: Coincident(g9,g10)
    c: Coincident(g10,g11)
    c: Coincident(g11,g12)
    c: Coincident(g12,g9)
    c: Horizontal(g9)
    c: Horizontal(g11)
    c: Vertical(g10)
    c: Vertical(g12)
    c: Coincident(g7,g10)
    c: Coincident(g11,g8)
    c: Coincident(g5,g9)
    c: Coincident(g6,g9)
    c: Symmetric(g5,g8,g-1)
    c: DistanceX(g9,g9) = 260
    c: DistanceX(g5) = 70
    c: DistanceY(g5) = 180
    c: Coincident(g2,g13)
    c: Horizontal(g13)
    c: Coincident(g13,g14)
    c: Coincident(g14,g15)
    c: DistanceX(g13,g13) = 184
    c: Distance(g15) = 142
    c: Coincident(g3,g16)
    c: Coincident(g1,g16)
    c: Vertical(g16)
    c: DistanceX(g1,g1) = 316
    c: Coincident(g0,g17)
    c: Coincident(g15,g17)
FEATURE [PartDesign::Pad] Pad016  label="Wall-2"
  Length = 8
  Length2 = 100
  Placement = pos=(0,0,16) rot=(0,0,1;0rad)
  Sketch = -> Sketch024
  Type = 0
FEATURE [Sketcher::SketchObject] Sketch025
  Placement = pos=(352,102,8) rot=(0,0,1;0.523599rad)
  sketch-geometry (7):
    g0: LineSegment StartX=0 StartY=5.7735 StartZ=0 EndX=-5 EndY=2.88675 EndZ=0
    g1: LineSegment StartX=-5 StartY=2.88675 StartZ=0 EndX=-5 EndY=-2.88675 EndZ=0
    g2: LineSegment StartX=-5 StartY=-2.88675 StartZ=0 EndX=0 EndY=-5.7735 EndZ=0
    g3: LineSegment StartX=0 StartY=-5.7735 StartZ=0 EndX=5 EndY=-2.88675 EndZ=0
    g4: LineSegment StartX=5 StartY=-2.88675 StartZ=0 EndX=5 EndY=2.88675 EndZ=0
    g5: LineSegment StartX=5 StartY=2.88675 StartZ=0 EndX=0 EndY=5.7735 EndZ=0
    g6: Circle [constr] CenterX=0 CenterY=0 CenterZ=0 NormalX=0 NormalY=0 NormalZ=1 Radius=5.7735
  constraints (16):
    c: Coincident(g0,g1)
    c: Coincident(g1,g2)
    c: Coincident(g2,g3)
    c: Coincident(g3,g4)
    c: Coincident(g4,g5)
    c: Coincident(g5,g0)
    c: Equal(g0, g1-g5) x5
    c: PointOnObject(g0,g6)
    c: PointOnObject(g1,g6)
    c: PointOnObject(g2,g6)
    c: PointOnObject(g3,g6)
    c: PointOnObject(g4,g6)
    c: PointOnObject(g5,g6)
    c: DistanceX(g-1,g3) = 5
    c: Coincident(g6,g-1)
    c: Vertical(g4)
FEATURE [PartDesign::Pad] Pad017  label="M6x20-base"
  Length = 4
  Length2 = 100
  Placement = pos=(352,102,8) rot=(0,0,1;0.523599rad)
  Sketch = -> Sketch025
  Type = 0
FEATURE [Sketcher::SketchObject] Sketch026
  Placement = pos=(352,102,12) rot=(0,0,1;0.523599rad)
  Support = -> Pad017 [Face8]
  sketch-geometry (1):
    g0: Circle CenterX=0 CenterY=0 CenterZ=0 NormalX=0 NormalY=0 NormalZ=1 Radius=2.9
  constraints (2):
    c: Coincident(g-1,g0)
    c: Radius(g0) = 2.9
FEATURE [PartDesign::Pad] Pad018  label="M6x20"
  Length = 19.8
  Length2 = 100
  Placement = pos=(352,102,8) rot=(0,0,1;0.523599rad)
  Sketch = -> Sketch026
  Type = 0
FEATURE [Spreadsheet::Sheet] Spreadsheet  label="Latskap"
  cells = A1=Thickness; B1(thickness)=8; A2=Height; B2(height)=400; A3=Width; B3(width)=400; A4=Depth; B4=400; A5=Inner; B5(inner)==height - 10 * thickness; A6=Wall inner; B6(wall_inner)==height - 2 * thickness; A7=Bolt distance; B7(bolt_distance)=260; A8=Bolt offset; B8(bolt_offset)==(wall_inner - 24) / 2; A9=Bolt pos; B9(bolt_pos)==(width - bolt_distance) / 2; A11=Arm offset; B11(arm_offset)=352; A12=Arm distance; B12(arm_distance)=38; A13=Arm lower; B13(arm_lower)=102; A14=Arm upper; B14(arm_upper)==arm_lower + arm_distance; A15=Arm thickness; B15(arm_thickness)=6; A16=Arm angle start; B16(arm_angle_start)=57; A19=Motor x; B19(motor_x)=246.8; A20=Motor y; B20(motor_y)=50.5; A22=Screen offset; B22==8 - 3.4
FEATURE [Sketcher::SketchObject] Sketch027
  Placement = pos=(0,0,8) rot=(1,0,0;3.14159rad)
  Support = -> Pad004 [Face11]
  expr: Constraints[9] = Latskap.bolt_offset
  expr: Constraints[8] = Latskap.bolt_distance
  sketch-geometry (10):
    g0: LineSegment [constr] StartX=70 StartY=180 StartZ=0 EndX=330 EndY=180 EndZ=0
    g1: LineSegment [constr] StartX=330 StartY=180 StartZ=0 EndX=330 EndY=-180 EndZ=0
    g2: LineSegment [constr] StartX=330 StartY=-180 StartZ=0 EndX=70 EndY=-180 EndZ=0
    g3: LineSegment [constr] StartX=70 StartY=-180 StartZ=0 EndX=70 EndY=180 EndZ=0
    g4: LineSegment [constr] StartX=70 StartY=180 StartZ=0 EndX=70 EndY=190 EndZ=0
    g5: LineSegment [constr] StartX=70 StartY=180 StartZ=0 EndX=78.6603 EndY=175 EndZ=0
    g6: LineSegment [constr] StartX=70 StartY=180 StartZ=0 EndX=61.3397 EndY=175 EndZ=0
    g7: LineSegment StartX=61.3397 StartY=175 StartZ=0 EndX=78.6603 EndY=175 EndZ=0
    g8: LineSegment StartX=78.6603 StartY=175 StartZ=0 EndX=70 EndY=190 EndZ=0
    g9: LineSegment StartX=70 StartY=190 StartZ=0 EndX=61.3397 EndY=175 EndZ=0
  constraints (27):
    c: Coincident(g0,g1)
    c: Coincident(g1,g2)
    c: Coincident(g2,g3)
    c: Coincident(g3,g0)
    c: Horizontal(g0)
    c: Horizontal(g2)
    c: Vertical(g1)
    c: Vertical(g3)
    c: DistanceX(g0,g0) = 260
    c: DistanceY(g0) = 180
    c: DistanceX(g0) = 70
    c: Coincident(g5,g0)
    c: Coincident(g5,g4)
    c: Coincident(g5,g6)
    c: Equal(g6,g4)
    c: Equal(g4,g5)
    c: Coincident(g7,g8)
    c: Coincident(g8,g9)
    c: Coincident(g6,g7)
    c: Coincident(g6,g9)
    c: Coincident(g4,g8)
    c: Coincident(g5,g7)
    c: Equal(g9,g7)
    c: Equal(g7,g8)
    c: Horizontal(g7)
    c: DistanceY(g5,g0) = 5
    c: Symmetric(g1,g0,g-1)
FEATURE [PartDesign::Pocket] Pocket002  label="Wall-1-4"
  Length = 4
  Placement = pos=(0,0,8) rot=(0,0,1;0rad)
  Sketch = -> Sketch027
  Type = 0
FEATURE [PartDesign::Mirrored] Mirrored
  MirrorPlane = -> Sketch027 [H_Axis]
  Placement = pos=(0,0,8) rot=(0,0,1;0rad)
FEATURE [PartDesign::LinearPattern] LinearPattern002
  Direction = -> Sketch027 [H_Axis]
  Length = 260
  Occurrences = 2
  Placement = pos=(0,0,8) rot=(0,0,1;0rad)
  expr: Length = Latskap.bolt_distance
FEATURE [PartDesign::MultiTransform] MultiTransform  label="Wall-1-3"
  Originals = -> [Pocket002]
  Placement = pos=(0,0,8) rot=(0,0,1;0rad)
  Transformations = -> [Mirrored,LinearPattern002]
FEATURE [Sketcher::SketchObject] Sketch028
  Placement = pos=(0,0,8) rot=(1,0,0;3.14159rad)
  Support = -> MultiTransform [Face4]
  expr: Constraints[30] = Latskap.arm_offset
  expr: Constraints[33] = -Latskap.arm_upper
  expr: Constraints[32] = -Latskap.arm_lower
  sketch-geometry (12):
    g0: LineSegment StartX=352 StartY=-94 StartZ=0 EndX=345.072 EndY=-106 EndZ=0
    g1: LineSegment StartX=345.072 StartY=-106 StartZ=0 EndX=358.928 EndY=-106 EndZ=0
    g2: LineSegment StartX=358.928 StartY=-106 StartZ=0 EndX=352 EndY=-94 EndZ=0
    g3: LineSegment StartX=352 StartY=-132 StartZ=0 EndX=345.072 EndY=-144 EndZ=0
    g4: LineSegment StartX=345.072 StartY=-144 StartZ=0 EndX=358.928 EndY=-144 EndZ=0
    g5: LineSegment StartX=358.928 StartY=-144 StartZ=0 EndX=352 EndY=-132 EndZ=0
    g6: LineSegment [constr] StartX=352 StartY=-132 StartZ=0 EndX=352 EndY=-140 EndZ=0
    g7: LineSegment [constr] StartX=345.072 StartY=-144 StartZ=0 EndX=352 EndY=-140 EndZ=0
    g8: LineSegment [constr] StartX=358.928 StartY=-144 StartZ=0 EndX=352 EndY=-140 EndZ=0
    g9: LineSegment [constr] StartX=352 StartY=-94 StartZ=0 EndX=352 EndY=-102 EndZ=0
    g10: LineSegment [constr] StartX=345.072 StartY=-106 StartZ=0 EndX=352 EndY=-102 EndZ=0
    g11: LineSegment [constr] StartX=358.928 StartY=-106 StartZ=0 EndX=352 EndY=-102 EndZ=0
  constraints (34):
    c: Coincident(g0,g1)
    c: Coincident(g1,g2)
    c: Coincident(g3,g4)
    c: Coincident(g4,g5)
    c: Coincident(g3,g5)
    c: Coincident(g0,g2)
    c: Coincident(g9,g10)
    c: Coincident(g9,g11)
    c: Coincident(g0,g9)
    c: Coincident(g0,g10)
    c: Coincident(g1,g11)
    c: Equal(g2,g0)
    c: Equal(g0,g1)
    c: Equal(g1,g3)
    c: Equal(g3,g5)
    c: Equal(g5,g4)
    c: Coincident(g6,g3)
    c: Coincident(g6,g7)
    c: Coincident(g6,g8)
    c: Coincident(g3,g7)
    c: Coincident(g4,g8)
    c: Equal(g6,g7)
    c: Equal(g7,g8)
    c: Equal(g8,g9)
    c: Equal(g9,g10)
    c: Equal(g10,g11)
    c: Horizontal(g1)
    c: Horizontal(g4)
    c: DistanceY(g0,g9) = 4
    c: DistanceY(g3,g6) = 4
    c: DistanceX(g9) = 352
    c: DistanceX(g6) = 352
    c: DistanceY(g9) = -102
    c: DistanceY(g6) = -140
FEATURE [PartDesign::Pocket] Pocket003  label="Wall-1-2"
  Length = 4
  Placement = pos=(0,0,8) rot=(0,0,1;0rad)
  Sketch = -> Sketch028
  Type = 0
FEATURE [Part::FeaturePython] Clone  label="Clone of M6x20"  # Draft clone (typed FeaturePython)
  Objects = -> [Pad018]
  Placement = pos=(70,180,8) rot=(0,0,1;0.523599rad)
  Scale = (1,1,1)
  expr: Placement.Base.y = Latskap.bolt_offset
  expr: Placement.Base.x = Latskap.bolt_pos
FEATURE [Part::FeaturePython] Array  label="Bolts-2"  # Draft array (typed FeaturePython)
  Angle = 360
  ArrayType = 0
  Axis = (0,0,1)
  Base = -> Clone
  Center = (0,0,0)
  Fuse = false
  IntervalAxis = (0,0,0)
  IntervalX = (260,0,0)
  IntervalY = (0,-360,0)
  IntervalZ = (0,0,0)
  NumberPolar = 1
  NumberX = 2
  NumberY = 2
  NumberZ = 1
  expr: IntervalX.x = Latskap.bolt_distance
  expr: IntervalY.y = -Latskap.bolt_offset * 2
FEATURE [Sketcher::SketchObject] Sketch029
  Placement = pos=(0,0,32) rot=(0,0,1;0rad)
  Support = -> Pad014 [Face9]
  expr: Constraints[11] = Latskap.bolt_offset
  expr: Constraints[9] = Latskap.bolt_pos
  expr: Constraints[8] = Latskap.bolt_distance
  sketch-geometry (8):
    g0: LineSegment [constr] StartX=70 StartY=180 StartZ=0 EndX=330 EndY=180 EndZ=0
    g1: LineSegment [constr] StartX=330 StartY=180 StartZ=0 EndX=330 EndY=-180 EndZ=0
    g2: LineSegment [constr] StartX=330 StartY=-180 StartZ=0 EndX=70 EndY=-180 EndZ=0
    g3: LineSegment [constr] StartX=70 StartY=-180 StartZ=0 EndX=70 EndY=180 EndZ=0
    g4: Circle CenterX=70 CenterY=180 CenterZ=0 NormalX=0 NormalY=0 NormalZ=1 Radius=10
    g5: Circle CenterX=330 CenterY=180 CenterZ=0 NormalX=0 NormalY=0 NormalZ=1 Radius=10
    g6: Circle CenterX=330 CenterY=-180 CenterZ=0 NormalX=0 NormalY=0 NormalZ=1 Radius=10
    g7: Circle CenterX=70 CenterY=-180 CenterZ=0 NormalX=0 NormalY=0 NormalZ=1 Radius=10
  constraints (16):
    c: Coincident(g0,g1)
    c: Coincident(g1,g2)
    c: Coincident(g2,g3)
    c: Coincident(g3,g0)
    c: Horizontal(g0)
    c: Horizontal(g2)
    c: Vertical(g1)
    c: Vertical(g3)
    c: DistanceX(g0,g0) = 260
    c: DistanceX(g0) = 70
    c: Symmetric(g0,g2,g-1)
    c: DistanceY(g0) = 180
    c: Equal(g7,g6)
    c: Equal(g6,g5)
    c: Equal(g5,g4)
    c: Radius(g5) = 10
FEATURE [PartDesign::Pocket] Pocket004  label="Wall-3-3"
  Length = 5
  Placement = pos=(0,0,32) rot=(0,0,1;0rad)
  Sketch = -> Sketch029
  Type = 0
FEATURE [Sketcher::SketchObject] Sketch030
  Placement = pos=(0,200,0) rot=(1,0,0;1.5708rad)
  expr: Constraints[9] = Latskap.width
  expr: Constraints[8] = Latskap.height
  sketch-geometry (4):
    g0: LineSegment StartX=0 StartY=0 StartZ=0 EndX=400 EndY=0 EndZ=0
    g1: LineSegment StartX=400 StartY=0 StartZ=0 EndX=400 EndY=400 EndZ=0
    g2: LineSegment StartX=400 StartY=400 StartZ=0 EndX=0 EndY=400 EndZ=0
    g3: LineSegment StartX=0 StartY=400 StartZ=0 EndX=0 EndY=0 EndZ=0
  constraints (11):
    c: Coincident(g0,g1)
    c: Coincident(g1,g2)
    c: Coincident(g2,g3)
    c: Coincident(g3,g0)
    c: Horizontal(g0)
    c: Horizontal(g2)
    c: Vertical(g1)
    c: Vertical(g3)
    c: DistanceY(g3,g3) = 400
    c: DistanceX(g2,g2) = 400
    c: Coincident(g0,g-1)
FEATURE [PartDesign::Pad] Pad019  label="Roof-straight"
  Length = 8
  Length2 = 100
  Placement = pos=(0,200,0) rot=(1,0,0;1.5708rad)
  Sketch = -> Sketch030
  Type = 0
FEATURE [PartDesign::Draft] Draft002  label="Roof"
  Angle = 45
  Base = -> Pad019 [Face2,Face1,Face3,Face4]
  NeutralPlane = -> Pad019 [Face5]
  Placement = pos=(0,200,0) rot=(1,0,0;1.5708rad)
  Reversed = true
FEATURE [Part::Mirroring] Part__Mirroring  label="Floor"
  Base = (200,1.52588e-05,200)
  Normal = (0,1,-1.19209e-07)
  Source = -> Draft002
FEATURE [Spreadsheet::Sheet] Spreadsheet001  label="Output"
  cells = A2==Floor.Shape.Volume
FEATURE [Part::Part2DObjectPython] InvoluteGear  label="Small-InvoluteGear"  # Draft 2D object (typed FeaturePython)
  ExternalGear = true
  HighPrecision = false
  Modules = 2.5
  NumberOfTeeth = 10
  Placement = pos=(246.8,50.5,22) rot=(0,0,1;0.034907rad)
  PressureAngle = 20
FEATURE [PartDesign::Pad] Pad  label="Small-gear-1"
  Length = 5
  Length2 = 100
  Placement = pos=(246.8,50.5,22) rot=(0,0,1;0.034907rad)
  Sketch = -> InvoluteGear
  Type = 0
FEATURE [Sketcher::SketchObject] Sketch031
  Placement = pos=(246.8,50.5,27) rot=(0,0,1;0.034907rad)
  Support = -> Pad [Face82]
  sketch-geometry (2):
    g0: ArcOfCircle CenterX=0 CenterY=0 CenterZ=0 NormalX=0 NormalY=0 NormalZ=1 Radius=2.9 StartAngle=3.7965 EndAngle=8.76987
    g1: LineSegment StartX=-2.3 StartY=1.76635 StartZ=0 EndX=-2.3 EndY=-1.76635 EndZ=0
  constraints (6):
    c: Vertical(g1)
    c: Coincident(g0,g1)
    c: Coincident(g0,g1)
    c: Radius(g0) = 2.9
    c: Coincident(g0,g-1)
    c: DistanceX(g0,g-1) = 2.3
FEATURE [Part::Part2DObjectPython] InvoluteGear001  label="Big-InvoluteGear001"  # Draft 2D object (typed FeaturePython)
  ExternalGear = true
  HighPrecision = false
  Modules = 2.5
  NumberOfTeeth = 100
  Placement = pos=(352,140,22) rot=(0,0,1;0.802851rad)
  PressureAngle = 20
  expr: Placement.Base.y = Latskap.arm_upper
  expr: Placement.Base.x = Latskap.arm_offset
FEATURE [PartDesign::Pad] Pad020  label="Big-gear-1"
  Length = 5
  Length2 = 100
  Placement = pos=(352,140,22) rot=(0,0,1;0.802851rad)
  Sketch = -> InvoluteGear001
  Type = 0
FEATURE [Sketcher::SketchObject] Sketch032
  Placement = pos=(352,140,27) rot=(0,0,1;0.802851rad)
  Support = -> Pad020 [Face602]
  sketch-geometry (12):
    g0: ArcOfCircle CenterX=0 CenterY=0 CenterZ=0 NormalX=0 NormalY=0 NormalZ=1 Radius=136 StartAngle=4.1444 EndAngle=9.3221
    g1: ArcOfCircle CenterX=0 CenterY=0 CenterZ=0 NormalX=0 NormalY=0 NormalZ=1 Radius=20 StartAngle=5.5676 EndAngle=7.89889
    g2: Circle CenterX=0 CenterY=0 CenterZ=0 NormalX=0 NormalY=0 NormalZ=1 Radius=2.5
    g3: Circle CenterX=-104.39 CenterY=-18.4067 CenterZ=0 NormalX=0 NormalY=0 NormalZ=1 Radius=2.5
    g4: LineSegment [constr] StartX=-104.39 StartY=-18.4067 StartZ=0 EndX=0 EndY=0 EndZ=0
    g5: LineSegment StartX=-135.284 StartY=13.9403 StartZ=0 EndX=-0.897932 EndY=19.9798 EndZ=0
    g6: LineSegment StartX=15.0942 StartY=-13.1212 StartZ=0 EndX=-0.444854 EndY=-30.9968 EndZ=0
    g7: LineSegment StartX=-73.1598 StartY=-114.646 StartZ=0 EndX=-10.9418 EndY=-43.0722 EndZ=0
    g8: ArcOfCircle CenterX=0 CenterY=0 CenterZ=0 NormalX=0 NormalY=0 NormalZ=1 Radius=31 StartAngle=3.71634 EndAngle=4.69804
    g9: ArcOfCircle CenterX=0 CenterY=0 CenterZ=0 NormalX=0 NormalY=0 NormalZ=1 Radius=44.4402 StartAngle=3.71634 EndAngle=4.46362
    g10: ArcOfCircle CenterX=-31.6597 CenterY=-20.5054 CenterZ=0 NormalX=0 NormalY=0 NormalZ=1 Radius=6.72011 StartAngle=0.574743 EndAngle=3.71634
    g11: LineSegment [constr] StartX=-0.444854 StartY=-30.9968 StartZ=0 EndX=-10.9418 EndY=-43.0722 EndZ=0
  constraints (33):
    c: Coincident(g0,g-1)
    c: Coincident(g0,g1)
    c: Angle(g-2,g1) = 1.51844
    c: Radius(g2) = 2.5
    c: Coincident(g2,g-1)
    c: Radius(g1) = 20
    c: Radius(g3) = 2.5
    c: Coincident(g4,g3)
    c: Coincident(g4,g-1)
    c: Angle(g4) = 0.174533
    c: Coincident(g5,g0)
    c: Coincident(g9,g7)
    c: Coincident(g10,g8)
    c: Coincident(g9,g10)
    c: Tangent(g10,g8)
    c: Tangent(g10,g9)
    c: Coincident(g6,g8)
    c: Tangent(g6,g1)
    c: Coincident(g0,g7)
    c: Coincident(g8,g-1)
    c: Coincident(g6,g1)
    c: Coincident(g9,g-1)
    c: Distance(g4) = 106
    c: Coincident(g5,g1)
    c: Tangent(g5,g1)
    c: Radius(g0) = 136
    c: Coincident(g11,g6)
    c: Coincident(g11,g7)
    c: Tangent(g11,g7)
    c: Tangent(g6,g11)
    c: Distance(g11) = 16
    c: Radius(g8) = 31
    c: Angle(g7) = 0.855211
FEATURE [PartDesign::Pocket] Pocket006  label="Big-gear"
  Length = 5
  Placement = pos=(352,140,22) rot=(0,0,1;0.802851rad)
  Sketch = -> Sketch032
  Type = 2
FEATURE [PartDesign::Pocket] Pocket007  label="Small-gear"
  Length = 5
  Placement = pos=(246.8,50.5,22) rot=(0,0,1;0.034907rad)
  Sketch = -> Sketch031
  Type = 2
FEATURE [Part::FeaturePython] Clone001  label="Clone of Pocket006"  # Draft clone (typed FeaturePython)
  Objects = -> [Pocket006]
  Placement = pos=(352,140,22) rot=(0,0,-1;0.122173rad)
  Scale = (1,1,1)
FEATURE [Sketcher::SketchObject] Sketch035
  Placement = pos=(352,102,8) rot=(0,0,1;0.523599rad)
  expr: Placement.Base.y = Latskap.arm_lower
  expr: Placement.Base.x = Latskap.arm_offset
  sketch-geometry (7):
    g0: LineSegment StartX=0 StartY=4.50333 StartZ=0 EndX=-3.9 EndY=2.25167 EndZ=0
    g1: LineSegment StartX=-3.9 StartY=2.25167 StartZ=0 EndX=-3.9 EndY=-2.25167 EndZ=0
    g2: LineSegment StartX=-3.9 StartY=-2.25167 StartZ=0 EndX=0 EndY=-4.50333 EndZ=0
    g3: LineSegment StartX=0 StartY=-4.50333 StartZ=0 EndX=3.9 EndY=-2.25167 EndZ=0
    g4: LineSegment StartX=3.9 StartY=-2.25167 StartZ=0 EndX=3.9 EndY=2.25167 EndZ=0
    g5: LineSegment StartX=3.9 StartY=2.25167 StartZ=0 EndX=0 EndY=4.50333 EndZ=0
    g6: Circle [constr] CenterX=0 CenterY=0 CenterZ=0 NormalX=0 NormalY=0 NormalZ=1 Radius=4.50333
  constraints (16):
    c: Coincident(g0,g1)
    c: Coincident(g1,g2)
    c: Coincident(g2,g3)
    c: Coincident(g3,g4)
    c: Coincident(g4,g5)
    c: Coincident(g5,g0)
    c: Equal(g0, g1-g5) x5
    c: PointOnObject(g0,g6)
    c: PointOnObject(g1,g6)
    c: PointOnObject(g2,g6)
    c: PointOnObject(g3,g6)
    c: PointOnObject(g4,g6)
    c: PointOnObject(g5,g6)
    c: DistanceX(g-1,g3) = 3.9
    c: Coincident(g6,g-1)
    c: Vertical(g4)
FEATURE [PartDesign::Pad] Pad021  label="M5x16-base"
  Length = 3.4
  Length2 = 100
  Placement = pos=(352,102,8) rot=(0,0,1;0.523599rad)
  Sketch = -> Sketch035
  Type = 0
FEATURE [Sketcher::SketchObject] Sketch034
  Placement = pos=(352,102,11.4) rot=(0,0,1;0.523599rad)
  Support = -> Pad021 [Face8]
  sketch-geometry (1):
    g0: Circle CenterX=0 CenterY=0 CenterZ=0 NormalX=0 NormalY=0 NormalZ=1 Radius=2.45
  constraints (2):
    c: Coincident(g-1,g0)
    c: Radius(g0) = 2.45
FEATURE [PartDesign::Pad] Pad022  label="M5x16"
  Length = 16
  Length2 = 100
  Placement = pos=(352,102,8) rot=(0,0,1;0.523599rad)
  Sketch = -> Sketch034
  Type = 0
FEATURE [Part::FeaturePython] Clone002  label="M5x16-upper"  # Draft clone (typed FeaturePython)
  Objects = -> [Pad022]
  Placement = pos=(352,140,8) rot=(0,0,1;0.523599rad)
  Scale = (1,1,1)
  expr: Placement.Base.y = Latskap.arm_upper
FEATURE [Sketcher::SketchObject] Sketch037
  Placement = pos=(0,0,24) rot=(1,0,0;3.14159rad)
  Support = -> Pocket004 [Face5]
  sketch-geometry (5):
    g0: ArcOfCircle CenterX=353.862 CenterY=-138.825 CenterZ=0 NormalX=0 NormalY=0 NormalZ=1 Radius=132.041 StartAngle=2.78042 EndAngle=3.47742
    g1: ArcOfCircle CenterX=352.946 CenterY=-140.459 CenterZ=0 NormalX=0 NormalY=0 NormalZ=1 Radius=130.128 StartAngle=1.31954 EndAngle=2.16446
    g2: LineSegment StartX=385.298 StartY=-14.4168 StartZ=0 EndX=371.961 EndY=-159.605 EndZ=0
    g3: LineSegment StartX=371.961 StartY=-159.605 StartZ=0 EndX=229.198 EndY=-182.338 EndZ=0
    g4: ArcOfCircle CenterX=254.068 CenterY=-61.3948 CenterZ=0 NormalX=0 NormalY=0 NormalZ=1 Radius=38.856 StartAngle=0.834801 EndAngle=4.05552
  constraints (5):
    c: Coincident(g2,g3)
    c: Coincident(g0,g4)
    c: Coincident(g1,g4)
    c: Coincident(g0,g3)
    c: Coincident(g1,g2)
FEATURE [PartDesign::Pocket] Pocket008  label="Wall-3"
  Length = 4
  Placement = pos=(0,0,32) rot=(0,0,1;0rad)
  Sketch = -> Sketch037
  Type = 0
FEATURE [Part::FeaturePython] Clone003  label="Clone of M5x16"  # Draft clone (typed FeaturePython)
  Objects = -> [Pad022]
  Placement = pos=(20,-153,8) rot=(0,0,1;0.523599rad)
  Scale = (1,1,1)
FEATURE [Part::FeaturePython] Array001  label="Down"  # Draft array (typed FeaturePython)
  Angle = 360
  ArrayType = 0
  Axis = (0,0,1)
  Base = -> Clone003
  Center = (0,0,0)
  Fuse = false
  IntervalAxis = (0,0,0)
  IntervalX = (1,0,0)
  IntervalY = (0,38,0)
  IntervalZ = (0,0,0)
  NumberPolar = 1
  NumberX = 1
  NumberY = 2
  NumberZ = 1
FEATURE [App::DocumentObjectGroup] Group003  label="Bolts"
  Group = -> [Clone002,Pad022,Array001,Pad021,Array]
FEATURE [Sketcher::SketchObject] Sketch038
  Placement = pos=(239.8,50.5,40) rot=(1,0,0;3.14159rad)
  Support = -> Revolution [Face5]
  sketch-geometry (1):
    g0: Circle CenterX=7 CenterY=0 CenterZ=0 NormalX=0 NormalY=0 NormalZ=1 Radius=3
  constraints (3):
    c: PointOnObject(g0,g-1)
    c: DistanceX(g-1,g0) = 7
    c: Radius(g0) = 3
FEATURE [PartDesign::Pad] Pad023  label="Motor"
  Length = 18
  Length2 = 100
  Placement = pos=(239.8,50.5,40) rot=(1,0,0;1.5708rad)
  Sketch = -> Sketch038
  Type = 0
FEATURE [Sketcher::SketchObject] Sketch039
  Placement = pos=(32,0,0) rot=(0.57735,0.57735,0.57735;2.0944rad)
  expr: Constraints[6] = Latskap.height - 2 * 8
  sketch-geometry (16):
    g0: LineSegment StartX=-192 StartY=8 StartZ=0 EndX=192 EndY=8 EndZ=0
    g1: LineSegment StartX=192 StartY=8 StartZ=0 EndX=192 EndY=392 EndZ=0
    g2: LineSegment StartX=192 StartY=392 StartZ=0 EndX=-192 EndY=392 EndZ=0
    g3: LineSegment StartX=-160 StartY=360 StartZ=0 EndX=160 EndY=360 EndZ=0
    g4: LineSegment StartX=160 StartY=360 StartZ=0 EndX=160 EndY=40 EndZ=0
    g5: LineSegment StartX=160 StartY=40 StartZ=0 EndX=-160 EndY=40 EndZ=0
    g6: LineSegment StartX=-160 StartY=40 StartZ=0 EndX=-160 EndY=360 EndZ=0
    g7: LineSegment StartX=-192 StartY=8 StartZ=0 EndX=-192 EndY=392 EndZ=0
    g8: LineSegment StartX=182 StartY=22 StartZ=0 EndX=-171.147 EndY=22 EndZ=0
    g9: LineSegment StartX=-171.147 StartY=22 StartZ=0 EndX=-171.147 EndY=16 EndZ=0
    g10: LineSegment StartX=-171.147 StartY=16 StartZ=0 EndX=182 EndY=16 EndZ=0
    g11: LineSegment StartX=182 StartY=16 StartZ=0 EndX=182 EndY=22 EndZ=0
    g12: LineSegment StartX=-158.178 StartY=384 StartZ=0 EndX=182 EndY=384 EndZ=0
    g13: LineSegment StartX=182 StartY=384 StartZ=0 EndX=182 EndY=378 EndZ=0
    g14: LineSegment StartX=182 StartY=378 StartZ=0 EndX=-158.178 EndY=378 EndZ=0
    g15: LineSegment StartX=-158.178 StartY=378 StartZ=0 EndX=-158.178 EndY=384 EndZ=0
  constraints (46):
    c: Coincident(g0,g1)
    c: Coincident(g1,g2)
    c: Horizontal(g0)
    c: Horizontal(g2)
    c: Vertical(g1)
    c: DistanceX(g2,g2) = 384
    c: DistanceY(g1,g1) = 384
    c: Symmetric(g0,g0,g-2)
    c: Coincident(g3,g4)
    c: Coincident(g4,g5)
    c: Coincident(g5,g6)
    c: Coincident(g6,g3)
    c: Horizontal(g3)
    c: Horizontal(g5)
    c: Vertical(g4)
    c: Vertical(g6)
    c: DistanceX(g3,g3) = 320
    c: DistanceY(g4,g4) = 320
    c: Symmetric(g5,g4,g-2)
    c: Vertical(g7)
    c: Coincident(g2,g7)
    c: Coincident(g7,g0)
    c: DistanceY(g0) = 8
    c: DistanceY(g4) = 40
    c: Coincident(g8,g9)
    c: Coincident(g9,g10)
    c: Coincident(g10,g11)
    c: Coincident(g11,g8)
    c: Horizontal(g8)
    c: Horizontal(g10)
    c: Vertical(g9)
    c: Vertical(g11)
    c: DistanceY(g11,g11) = 6
    c: DistanceY(g0,g9) = 8
    c: DistanceX(g10,g0) = 10
    c: Coincident(g12,g13)
    c: Coincident(g13,g14)
    c: Coincident(g14,g15)
    c: Coincident(g15,g12)
    c: Horizontal(g12)
    c: Horizontal(g14)
    c: Vertical(g13)
    c: Vertical(g15)
    c: DistanceY(g12,g2) = 8
    c: DistanceY(g15,g15) = 6
    c: DistanceX(g12,g1) = 10
FEATURE [PartDesign::Pad] Pad024  label="Front"
  Length = 8
  Length2 = 100
  Placement = pos=(32,0,0) rot=(0.57735,0.57735,0.57735;2.0944rad)
  Sketch = -> Sketch039
  Type = 0
FEATURE [Part::FeaturePython] Clone004  label="Clone of Door-side-1"  # Draft clone (typed FeaturePython)
  Objects = -> [LinearPattern001]
  Placement = pos=(-71,367,8) rot=(0,0,1;0rad)
  Scale = (1,1,1)
FEATURE [App::DocumentObjectGroup] Group  label="Clones"
  Group = -> [Clone2D,Clone2D001,Clone001,Clone004]
FEATURE [Sketcher::SketchObject] Sketch040
  ExternalGeometry = -> [Pad015]
  Placement = pos=(0,0,40) rot=(0,0,1;0rad)
  Support = -> Pad015 [Face13]
  sketch-geometry (8):
    g0: LineSegment StartX=40 StartY=168.1 StartZ=0 EndX=380 EndY=168.1 EndZ=0
    g1: LineSegment StartX=380 StartY=168.1 StartZ=0 EndX=380 EndY=160 EndZ=0
    g2: LineSegment StartX=380 StartY=160 StartZ=0 EndX=40 EndY=160 EndZ=0
    g3: LineSegment StartX=40 StartY=160 StartZ=0 EndX=40 EndY=168.1 EndZ=0
    g4: LineSegment StartX=40 StartY=-160 StartZ=0 EndX=380 EndY=-160 EndZ=0
    g5: LineSegment StartX=380 StartY=-160 StartZ=0 EndX=380 EndY=-168.1 EndZ=0
    g6: LineSegment StartX=380 StartY=-168.1 StartZ=0 EndX=40 EndY=-168.1 EndZ=0
    g7: LineSegment StartX=40 StartY=-168.1 StartZ=0 EndX=40 EndY=-160 EndZ=0
  constraints (24):
    c: Coincident(g0,g1)
    c: Coincident(g1,g2)
    c: Coincident(g2,g3)
    c: Coincident(g3,g0)
    c: Horizontal(g0)
    c: Horizontal(g2)
    c: Vertical(g1)
    c: Vertical(g3)
    c: Coincident(g4,g5)
    c: Coincident(g5,g6)
    c: Coincident(g6,g7)
    c: Coincident(g7,g4)
    c: Horizontal(g4)
    c: Horizontal(g6)
    c: Vertical(g5)
    c: Vertical(g7)
    c: DistanceY(g7,g7) = 8.1
    c: PointOnObject(g4,g-3)
    c: DistanceY(g3,g3) = 8.1
    c: PointOnObject(g2,g-3)
    c: PointOnObject(g1,g-4)
    c: PointOnObject(g4,g-4)
    c: DistanceY(g2,g-3) = 32
    c: DistanceY(g-3,g4) = 32
FEATURE [PartDesign::Pocket] Pocket009  label="Wall-inner"
  Length = 4.1
  Placement = pos=(0,0,40) rot=(0,0,1;0rad)
  Sketch = -> Sketch040
  Type = 0
FEATURE [Part::Part2DObjectPython] Shape2DView  label="sWall-0"  # Draft 2D object (typed FeaturePython)
  Base = -> Draft
  FaceNumbers = [4]
  HiddenLines = false
  Placement = pos=(20,220,0) rot=(0,0,1;0rad)
  Projection = (0,0,1)
  ProjectionMode = 0
  SegmentLength = 0.05
  Tessellation = false
FEATURE [Part::Part2DObjectPython] Shape2DView002  label="sWall-1"  # Draft 2D object (typed FeaturePython)
  Base = -> Pocket003
  FaceNumbers = [3]
  HiddenLines = false
  Placement = pos=(841,222,0) rot=(0,0,1;0rad)
  Projection = (0,0,-1)
  ProjectionMode = 0
  SegmentLength = 0.05
  Tessellation = false
FEATURE [Sketcher::SketchObject] Sketch041
  Placement = pos=(384,0,400) rot=(0.57735,0.57735,0.57735;2.0944rad)
  expr: Constraints[5] = (400 - 320) / 2
  sketch-geometry (21):
    g0: LineSegment StartX=-192 StartY=-40 StartZ=0 EndX=192 EndY=-40 EndZ=0
    g1: LineSegment StartX=192 StartY=-360 StartZ=0 EndX=-192 EndY=-360 EndZ=0
    g2: LineSegment StartX=192 StartY=-40 StartZ=0 EndX=192 EndY=-170 EndZ=0
    g3: LineSegment StartX=192 StartY=-170 StartZ=0 EndX=172 EndY=-170 EndZ=0
    g4: LineSegment StartX=172 StartY=-170 StartZ=0 EndX=172 EndY=-230 EndZ=0
    g5: LineSegment StartX=172 StartY=-230 StartZ=0 EndX=192 EndY=-230 EndZ=0
    g6: LineSegment StartX=192 StartY=-230 StartZ=0 EndX=192 EndY=-360 EndZ=0
    g7: LineSegment StartX=-192 StartY=-40 StartZ=0 EndX=-192 EndY=-170 EndZ=0
    g8: LineSegment StartX=-192 StartY=-170 StartZ=0 EndX=-172 EndY=-170 EndZ=0
    g9: LineSegment StartX=-172 StartY=-170 StartZ=0 EndX=-172 EndY=-230 EndZ=0
    g10: LineSegment StartX=-172 StartY=-230 StartZ=0 EndX=-192 EndY=-230 EndZ=0
    g11: LineSegment StartX=-192 StartY=-230 StartZ=0 EndX=-192 EndY=-360 EndZ=0
    g12: LineSegment [constr] StartX=-182 StartY=-70 StartZ=0 EndX=182 EndY=-70 EndZ=0
    g13: LineSegment [constr] StartX=182 StartY=-70 StartZ=0 EndX=182 EndY=-330 EndZ=0
    g14: LineSegment [constr] StartX=182 StartY=-330 StartZ=0 EndX=-182 EndY=-330 EndZ=0
    g15: LineSegment [constr] StartX=-182 StartY=-330 StartZ=0 EndX=-182 EndY=-70 EndZ=0
    g16: LineSegment [constr] StartX=-172 StartY=-200 StartZ=0 EndX=172 EndY=-200 EndZ=0
    g17: Circle CenterX=-182 CenterY=-70 CenterZ=0 NormalX=0 NormalY=0 NormalZ=1 Radius=3
    g18: Circle CenterX=182 CenterY=-70 CenterZ=0 NormalX=0 NormalY=0 NormalZ=1 Radius=3
    g19: Circle CenterX=182 CenterY=-330 CenterZ=0 NormalX=0 NormalY=0 NormalZ=1 Radius=3
    g20: Circle CenterX=-182 CenterY=-330 CenterZ=0 NormalX=0 NormalY=0 NormalZ=1 Radius=3
  constraints (60):
    c: Horizontal(g0)
    c: Horizontal(g1)
    c: Symmetric(g1,g1,g-2)
    c: DistanceX(g1,g1) = 384
    c: DistanceY(g1,g0) = 320
    c: DistanceY(g0,g-1) = 40
    c: Coincident(g2,g3)
    c: Coincident(g3,g4)
    c: Coincident(g4,g5)
    c: Coincident(g5,g6)
    c: Coincident(g1,g6)
    c: Horizontal(g5)
    c: Horizontal(g3)
    c: Vertical(g4)
    c: Vertical(g2)
    c: Vertical(g6)
    c: Equal(g2,g6)
    c: Coincident(g7,g8)
    c: Coincident(g8,g9)
    c: Coincident(g9,g10)
    c: Coincident(g10,g11)
    c: Coincident(g1,g11)
    c: Horizontal(g10)
    c: Horizontal(g8)
    c: Vertical(g9)
    c: Vertical(g11)
    c: Vertical(g7)
    c: Equal(g7,g11)
    c: Equal(g11,g2)
    c: Equal(g8,g10)
    c: Equal(g10,g3)
    c: Coincident(g0,g2)
    c: Equal(g3,g5)
    c: Coincident(g0,g7)
    c: DistanceX(g8,g8) = 20
    c: DistanceY(g9,g9) = 60
    c: Coincident(g12,g13)
    c: Coincident(g13,g14)
    c: Coincident(g14,g15)
    c: Coincident(g15,g12)
    c: Horizontal(g12)
    c: Horizontal(g14)
    c: Vertical(g13)
    c: Vertical(g15)
    c: Horizontal(g16)
    c: PointOnObject(g16,g4)
    c: PointOnObject(g16,g9)
    c: DistanceY(g16) = -200
    c: DistanceY(g13,g13) = 260
    c: DistanceX(g14,g14) = 364
    c: Symmetric(g13,g14,g-2)
    c: Symmetric(g12,g13,g16)
    c: Equal(g20,g17)
    c: Equal(g17,g18)
    c: Equal(g18,g19)
    c: Radius(g18) = 3
    c: Coincident(g17,g12)
    c: Coincident(g14,g20)
    c: Coincident(g19,g13)
    c: Coincident(g18,g12)
FEATURE [PartDesign::Pad] Pad025  label="Back-2-1"
  Length = 8
  Length2 = 100
  Placement = pos=(384,0,400) rot=(0.57735,0.57735,0.57735;2.0944rad)
  Reversed = true
  Sketch = -> Sketch041
  Type = 0
FEATURE [Sketcher::SketchObject] Sketch042
  Placement = pos=(0,0,36) rot=(0,0,1;0rad)
  sketch-geometry (4):
    g0: LineSegment StartX=40 StartY=-160.1 StartZ=0 EndX=380 EndY=-160.1 EndZ=0
    g1: LineSegment StartX=380 StartY=-160.1 StartZ=0 EndX=380 EndY=-168.1 EndZ=0
    g2: LineSegment StartX=380 StartY=-168.1 StartZ=0 EndX=40 EndY=-168.1 EndZ=0
    g3: LineSegment StartX=40 StartY=-168.1 StartZ=0 EndX=40 EndY=-160.1 EndZ=0
  constraints (11):
    c: Coincident(g0,g1)
    c: Coincident(g1,g2)
    c: Coincident(g2,g3)
    c: Coincident(g3,g0)
    c: Horizontal(g0)
    c: Horizontal(g2)
    c: Vertical(g1)
    c: Vertical(g3)
    c: DistanceY(g1,g1) = 8
    c: DistanceX(g0) = 40
    c: DistanceY(g0) = -160.1
FEATURE [PartDesign::Pad] Pad026  label="Floor-inner-1"
  Length = 328
  Length2 = 100
  Placement = pos=(0,0,36) rot=(0,0,1;0rad)
  Sketch = -> Sketch042
  Type = 0
  expr: Length = Latskap001.inner + 8
FEATURE [Part::FeaturePython] Clone005  label="Roof-inner"  # Draft clone (typed FeaturePython)
  Objects = -> [Pad026]
  Placement = pos=(0,328,36) rot=(0,0,1;0rad)
  Scale = (1,1,1)
FEATURE [Part::Mirroring] Part__Mirroring001  label="Wall-outer-draft (Mirror #2)"
  Base = (0,0,0)
  Normal = (0,0,1)
  Placement = pos=(0,0,400) rot=(0,0,1;0rad)
  Source = -> Draft
FEATURE [Part::Mirroring] Part__Mirroring002  label="Wall-1 (Mirror #3)"
  Base = (216,0,200)
  Normal = (0,0,1)
  Source = -> Pocket003
FEATURE [PartDesign::Draft] Draft003  label="Door-Draft003"
  Angle = 45
  Base = -> Pad008 [Face5,Face1,Face6,Face3]
  NeutralPlane = -> Pad008 [Face2]
  Reversed = true
FEATURE [Sketcher::SketchObject] Sketch043
  Placement = pos=(8,0,0) rot=(0.57735,0.57735,0.57735;2.0944rad)
  Support = -> Draft003 [Face4]
  sketch-geometry (5):
    g0: LineSegment StartX=-39 StartY=274.6 StartZ=0 EndX=39 EndY=274.6 EndZ=0
    g1: LineSegment StartX=39 StartY=274.6 StartZ=0 EndX=39 EndY=134.6 EndZ=0
    g2: LineSegment StartX=39 StartY=134.6 StartZ=0 EndX=-39 EndY=134.6 EndZ=0
    g3: LineSegment StartX=-39 StartY=134.6 StartZ=0 EndX=-39 EndY=274.6 EndZ=0
    g4: LineSegment [constr] StartX=-39 StartY=200 StartZ=0 EndX=39 EndY=200 EndZ=0
  constraints (16):
    c: Coincident(g0,g1)
    c: Coincident(g1,g2)
    c: Coincident(g2,g3)
    c: Coincident(g3,g0)
    c: Horizontal(g0)
    c: Horizontal(g2)
    c: Vertical(g1)
    c: Vertical(g3)
    c: DistanceX(g2,g2) = 78
    c: Symmetric(g2,g1,g-2)
    c: DistanceY(g1,g1) = 140
    c: Horizontal(g4)
    c: PointOnObject(g4,g3)
    c: PointOnObject(g4,g1)
    c: DistanceY(g4) = 200
    c: DistanceY(g2,g4) = 65.4
FEATURE [Mesh::Feature] All  label="MangaScreen"
  Placement = pos=(0,0,200) rot=(0,1,0;1.5708rad)
FEATURE [Sketcher::SketchObject] Sketch045
  Placement = pos=(8,0,0) rot=(0.57735,0.57735,0.57735;2.0944rad)
  expr: Constraints[22] = (400 - 260) / 2
  sketch-geometry (22):
    g0: LineSegment StartX=88 StartY=384 StartZ=0 EndX=88 EndY=16 EndZ=0
    g1: LineSegment StartX=-192 StartY=40 StartZ=0 EndX=-192 EndY=360 EndZ=0
    g2: LineSegment StartX=-192 StartY=40 StartZ=0 EndX=-170 EndY=40 EndZ=0
    g3: LineSegment StartX=-85 StartY=16 StartZ=0 EndX=88 EndY=16 EndZ=0
    g4: LineSegment StartX=88 StartY=384 StartZ=0 EndX=-85 EndY=384 EndZ=0
    g5: LineSegment StartX=-170 StartY=360 StartZ=0 EndX=-192 EndY=360 EndZ=0
    g6: LineSegment StartX=-85 StartY=330 StartZ=0 EndX=55 EndY=330 EndZ=0
    g7: LineSegment StartX=55 StartY=330 StartZ=0 EndX=55 EndY=70 EndZ=0
    g8: LineSegment StartX=55 StartY=70 StartZ=0 EndX=-85 EndY=70 EndZ=0
    g9: LineSegment StartX=-170 StartY=40 StartZ=0 EndX=-170 EndY=360 EndZ=0
    g10: LineSegment StartX=-85 StartY=384 StartZ=0 EndX=-85 EndY=330 EndZ=0
    g11: LineSegment StartX=-85 StartY=70 StartZ=0 EndX=-85 EndY=16 EndZ=0
    g12: Circle CenterX=-182 CenterY=340 CenterZ=0 NormalX=0 NormalY=0 NormalZ=1 Radius=2.5
    g13: Circle CenterX=-182 CenterY=60 CenterZ=0 NormalX=0 NormalY=0 NormalZ=1 Radius=2.5
    g14: Circle CenterX=-62 CenterY=340 CenterZ=0 NormalX=0 NormalY=0 NormalZ=1 Radius=2.5
    g15: Circle CenterX=68 CenterY=340 CenterZ=0 NormalX=0 NormalY=0 NormalZ=1 Radius=2.5
    g16: Circle CenterX=68 CenterY=60 CenterZ=0 NormalX=0 NormalY=0 NormalZ=1 Radius=2.5
    g17: Circle CenterX=-62 CenterY=60 CenterZ=0 NormalX=0 NormalY=0 NormalZ=1 Radius=2.5
    g18: LineSegment [constr] StartX=68 StartY=340 StartZ=0 EndX=-182 EndY=340 EndZ=0
    g19: LineSegment [constr] StartX=-182 StartY=340 StartZ=0 EndX=-182 EndY=60 EndZ=0
    g20: LineSegment [constr] StartX=-182 StartY=60 StartZ=0 EndX=68 EndY=60 EndZ=0
    g21: LineSegment [constr] StartX=68 StartY=60 StartZ=0 EndX=68 EndY=340 EndZ=0
  constraints (63):
    c: Vertical(g0)
    c: Vertical(g1)
    c: DistanceY(g1) = 40
    c: DistanceX(g1,g0) = 280
    c: DistanceY(g1,g1) = 320
    c: DistanceX(g1) = -192
    c: Coincident(g0,g3)
    c: Coincident(g1,g2)
    c: Horizontal(g2)
    c: Horizontal(g3)
    c: DistanceY(g0,g0) = 368
    c: Coincident(g1,g5)
    c: Coincident(g0,g4)
    c: Horizontal(g4)
    c: Horizontal(g5)
    c: Equal(g5,g2)
    c: Equal(g4,g3)
    c: Coincident(g6,g7)
    c: Coincident(g7,g8)
    c: Horizontal(g6)
    c: Horizontal(g8)
    c: Vertical(g7)
    c: DistanceY(g8) = 70
    c: DistanceY(g7,g7) = 260
    c: DistanceX(g-1,g7) = 55
    c: DistanceX(g8,g8) = 140
    c: Vertical(g9)
    c: Coincident(g5,g9)
    c: Coincident(g2,g9)
    c: DistanceX(g5,g5) = 22
    c: DistanceY(g3) = 16
    c: Coincident(g10,g4)
    c: Coincident(g10,g6)
    c: Vertical(g10)
    c: Coincident(g11,g8)
    c: Coincident(g11,g3)
    c: Vertical(g11)
    c: Equal(g15,g16)
    c: Equal(g16,g17)
    c: Equal(g17,g13)
    c: Equal(g13,g12)
    c: Equal(g12,g14)
    c: Radius(g15) = 2.5
    c: Coincident(g18,g19)
    c: Coincident(g19,g20)
    c: Coincident(g20,g21)
    c: Coincident(g21,g18)
    c: Horizontal(g18)
    c: Horizontal(g20)
    c: Vertical(g19)
    c: Vertical(g21)
    c: Coincident(g13,g19)
    c: Coincident(g18,g12)
    c: PointOnObject(g14,g18)
    c: Coincident(g15,g18)
    c: Coincident(g16,g20)
    c: PointOnObject(g17,g20)
    c: DistanceY(g21,g21) = 280
    c: DistanceY(g13) = 60
    c: DistanceX(g12) = -182
    c: DistanceX(g18,g18) = 250
    c: DistanceX(g13,g17) = 120
    c: DistanceX(g12,g14) = 120
FEATURE [PartDesign::Pad] Pad027  label="Door-1"
  Length = 8
  Length2 = 100
  Placement = pos=(8,0,0) rot=(0.57735,0.57735,0.57735;2.0944rad)
  Sketch = -> Sketch045
  Type = 0
FEATURE [Part::Mirroring] Part__Mirroring003  label="Door-side-1 (Mirror #4)"
  Base = (0,0,200)
  Normal = (0,0,1)
  Source = -> LinearPattern001
FEATURE [Sketcher::SketchObject] Sketch047
  Placement = pos=(16,0,0) rot=(0.57735,0.57735,0.57735;2.0944rad)
  sketch-geometry (27):
    g0: LineSegment StartX=-192 StartY=360 StartZ=0 EndX=-85 EndY=360 EndZ=0
    g1: LineSegment StartX=-85 StartY=360 StartZ=0 EndX=-85 EndY=384 EndZ=0
    g2: LineSegment StartX=-85 StartY=384 StartZ=0 EndX=88 EndY=384 EndZ=0
    g3: LineSegment StartX=88 StartY=384 StartZ=0 EndX=88 EndY=16 EndZ=0
    g4: LineSegment StartX=88 StartY=16 StartZ=0 EndX=-85 EndY=16 EndZ=0
    g5: LineSegment StartX=-85 StartY=16 StartZ=0 EndX=-85 EndY=40 EndZ=0
    g6: LineSegment StartX=-85 StartY=40 StartZ=0 EndX=-192 EndY=40 EndZ=0
    g7: LineSegment StartX=-192 StartY=40 StartZ=0 EndX=-192 EndY=360 EndZ=0
    g8: LineSegment [constr] StartX=-182 StartY=340 StartZ=0 EndX=68 EndY=340 EndZ=0
    g9: LineSegment [constr] StartX=68 StartY=340 StartZ=0 EndX=68 EndY=60 EndZ=0
    g10: LineSegment [constr] StartX=68 StartY=60 StartZ=0 EndX=-182 EndY=60 EndZ=0
    g11: LineSegment [constr] StartX=-182 StartY=60 StartZ=0 EndX=-182 EndY=340 EndZ=0
    g12: Circle CenterX=-182 CenterY=340 CenterZ=0 NormalX=0 NormalY=0 NormalZ=1 Radius=2.5
    g13: Circle CenterX=68 CenterY=340 CenterZ=0 NormalX=0 NormalY=0 NormalZ=1 Radius=2.5
    g14: Circle CenterX=68 CenterY=60 CenterZ=0 NormalX=0 NormalY=0 NormalZ=1 Radius=2.5
    g15: Circle CenterX=-182 CenterY=60 CenterZ=0 NormalX=0 NormalY=0 NormalZ=1 Radius=2.5
    g16: Circle CenterX=-62 CenterY=340 CenterZ=0 NormalX=0 NormalY=0 NormalZ=1 Radius=2.5
    g17: Circle CenterX=-62 CenterY=60 CenterZ=0 NormalX=0 NormalY=0 NormalZ=1 Radius=2.5
    g18: LineSegment [constr] StartX=-25 StartY=225 StartZ=0 EndX=25 EndY=225 EndZ=0
    g19: LineSegment [constr] StartX=25 StartY=225 StartZ=0 EndX=25 EndY=175 EndZ=0
    g20: LineSegment [constr] StartX=25 StartY=175 StartZ=0 EndX=-25 EndY=175 EndZ=0
    g21: LineSegment [constr] StartX=-25 StartY=175 StartZ=0 EndX=-25 EndY=225 EndZ=0
    g22: LineSegment [constr] StartX=-81.6408 StartY=200 StartZ=0 EndX=58.515 EndY=200 EndZ=0
    g23: Circle CenterX=-25 CenterY=225 CenterZ=0 NormalX=0 NormalY=0 NormalZ=1 Radius=2
    g24: Circle CenterX=25 CenterY=225 CenterZ=0 NormalX=0 NormalY=0 NormalZ=1 Radius=2
    g25: Circle CenterX=25 CenterY=175 CenterZ=0 NormalX=0 NormalY=0 NormalZ=1 Radius=2
    g26: Circle CenterX=-25 CenterY=175 CenterZ=0 NormalX=0 NormalY=0 NormalZ=1 Radius=2
  constraints (72):
    c: Horizontal(g0)
    c: Coincident(g0,g1)
    c: Coincident(g1,g2)
    c: Horizontal(g2)
    c: Coincident(g2,g3)
    c: Vertical(g3)
    c: Coincident(g3,g4)
    c: Horizontal(g4)
    c: Coincident(g4,g5)
    c: Vertical(g5)
    c: Coincident(g5,g6)
    c: Horizontal(g6)
    c: Coincident(g6,g7)
    c: Coincident(g7,g0)
    c: Vertical(g7)
    c: Vertical(g1)
    c: DistanceY(g3,g3) = 368
    c: DistanceY(g7,g7) = 320
    c: Equal(g6,g0)
    c: Equal(g1,g5)
    c: DistanceX(g6) = -192
    c: DistanceY(g6) = 40
    c: DistanceX(g4,g4) = 173
    c: DistanceX(g6,g6) = 107
    c: Coincident(g8,g9)
    c: Coincident(g9,g10)
    c: Coincident(g10,g11)
    c: Coincident(g11,g8)
    c: Horizontal(g8)
    c: Horizontal(g10)
    c: Vertical(g9)
    c: Vertical(g11)
    c: Coincident(g12,g8)
    c: Coincident(g13,g8)
    c: Coincident(g14,g9)
    c: Coincident(g15,g10)
    c: PointOnObject(g16,g8)
    c: PointOnObject(g17,g10)
    c: Equal(g12,g16)
    c: Equal(g16,g13)
    c: Equal(g13,g14)
    c: Equal(g14,g17)
    c: Equal(g17,g15)
    c: Radius(g13) = 2.5
    c: DistanceY(g9,g9) = 280
    c: DistanceX(g8,g8) = 250
    c: DistanceX(g8) = 68
    c: DistanceY(g9) = 60
    c: Coincident(g18,g19)
    c: Coincident(g19,g20)
    c: Coincident(g20,g21)
    c: Coincident(g21,g18)
    c: Horizontal(g18)
    c: Horizontal(g20)
    c: Vertical(g19)
    c: Vertical(g21)
    c: Equal(g18,g19)
    c: DistanceX(g18,g18) = 50
    c: Symmetric(g18,g18,g-2)
    c: Horizontal(g22)
    c: DistanceY(g22) = 200
    c: Symmetric(g18,g19,g22)
    c: Coincident(g23,g18)
    c: Coincident(g24,g18)
    c: Coincident(g25,g19)
    c: Coincident(g26,g20)
    c: Equal(g26,g23)
    c: Equal(g23,g24)
    c: Equal(g24,g25)
    c: Radius(g24) = 2
    c: DistanceX(g10,g17) = 120
    c: DistanceX(g8,g16) = 120
FEATURE [PartDesign::Pad] Pad029  label="Door-2-1"
  Length = 8
  Length2 = 100
  Placement = pos=(16,0,0) rot=(0.57735,0.57735,0.57735;2.0944rad)
  Sketch = -> Sketch047
  Type = 0
FEATURE [Sketcher::SketchObject] Sketch048
  Placement = pos=(16,0,0) rot=(0.57735,0.57735,-0.57735;4.18879rad)
  Support = -> Pad029 [Face15]
  sketch-geometry (5):
    g0: LineSegment StartX=-35 StartY=-165 StartZ=0 EndX=35 EndY=-165 EndZ=0
    g1: LineSegment StartX=35 StartY=-165 StartZ=0 EndX=35 EndY=-235 EndZ=0
    g2: LineSegment StartX=35 StartY=-235 StartZ=0 EndX=-35 EndY=-235 EndZ=0
    g3: LineSegment StartX=-35 StartY=-235 StartZ=0 EndX=-35 EndY=-165 EndZ=0
    g4: LineSegment [constr] StartX=-157.486 StartY=-200 StartZ=0 EndX=122.257 EndY=-200 EndZ=0
  constraints (14):
    c: Coincident(g0,g1)
    c: Coincident(g1,g2)
    c: Coincident(g2,g3)
    c: Coincident(g3,g0)
    c: Horizontal(g0)
    c: Horizontal(g2)
    c: Vertical(g1)
    c: Vertical(g3)
    c: Equal(g3,g0)
    c: Symmetric(g0,g0,g-2)
    c: Horizontal(g4)
    c: Symmetric(g0,g1,g4)
    c: DistanceY(g4) = -200
    c: DistanceX(g0,g0) = 70
FEATURE [PartDesign::Pocket] Pocket012  label="Door-2"
  Length = 4
  Placement = pos=(16,0,0) rot=(0.57735,0.57735,0.57735;2.0944rad)
  Sketch = -> Sketch048
  Type = 0
FEATURE [Part::Part2DObjectPython] Shape2DView003  label="sWall-2"  # Draft 2D object (typed FeaturePython)
  Base = -> Pad016
  HiddenLines = false
  Placement = pos=(229,830.287,0) rot=(0,0,1;1.5708rad)
  Projection = (0,0,1)
  ProjectionMode = 0
  SegmentLength = 0.05
  Tessellation = false
FEATURE [Part::Part2DObjectPython] Shape2DView006  label="sWall-3"  # Draft 2D object (typed FeaturePython)
  Base = -> Pocket008
  FaceNumbers = [4]
  HiddenLines = false
  Placement = pos=(1218,220.337,0) rot=(0,0,1;0rad)
  Projection = (0,0,-1)
  ProjectionMode = 0
  SegmentLength = 0.05
  Tessellation = false
FEATURE [Part::Part2DObjectPython] Shape2DView007  label="sWall-4"  # Draft 2D object (typed FeaturePython)
  Base = -> Pocket009
  HiddenLines = false
  Placement = pos=(1191,222.026,0) rot=(0,0,1;0rad)
  Projection = (0,0,1)
  ProjectionMode = 0
  SegmentLength = 0.05
  Tessellation = false
FEATURE [Part::Part2DObjectPython] Rectangle  label="Valchromat"  # Draft 2D object (typed FeaturePython)
  ChamferSize = 0
  Columns = 1
  FilletRadius = 0
  Height = 1250
  Length = 2500
  MakeFace = false
  Rows = 1
FEATURE [Part::Part2DObjectPython] Shape2DView010  label="sDoor-1"  # Draft 2D object (typed FeaturePython)
  Base = -> Pad027
  FaceNumbers = [13]
  HiddenLines = false
  Placement = pos=(2021.19,984,0) rot=(0,0,1;0rad)
  Projection = (1,0,0)
  ProjectionMode = 0
  SegmentLength = 0.05
  Tessellation = false
FEATURE [Part::Part2DObjectPython] Shape2DView013  label="sDoor-side-0"  # Draft 2D object (typed FeaturePython)
  Base = -> Part__Mirroring003
  FaceNumbers = [3]
  HiddenLines = false
  Placement = pos=(136,1047.02,0) rot=(0,0,1;0rad)
  Projection = (0,0,1)
  ProjectionMode = 0
  SegmentLength = 0.05
  Tessellation = false
FEATURE [Part::Part2DObjectPython] Shape2DView014  label="sDoor-side-1"  # Draft 2D object (typed FeaturePython)
  Base = -> LinearPattern001
  HiddenLines = false
  Placement = pos=(224,1047.02,0) rot=(0,0,1;0rad)
  Projection = (0,0,-1)
  ProjectionMode = 0
  SegmentLength = 0.05
  Tessellation = false
FEATURE [Sketcher::SketchObject] Sketch049
  Placement = pos=(0,0,16) rot=(0,0,1;0rad)
  Support = -> Pocket003 [Face5]
  sketch-geometry (8):
    g0: LineSegment StartX=283.177 StartY=-35.5949 StartZ=0 EndX=272.012 EndY=-52.7877 EndZ=0
    g1: LineSegment StartX=272.012 StartY=-52.7877 StartZ=0 EndX=281.237 EndY=-58.7787 EndZ=0
    g2: LineSegment StartX=281.237 StartY=-58.7787 StartZ=0 EndX=292.402 EndY=-41.586 EndZ=0
    g3: LineSegment StartX=292.402 StartY=-41.586 StartZ=0 EndX=283.177 EndY=-35.5949 EndZ=0
    g4: LineSegment StartX=142.836 StartY=163.034 StartZ=0 EndX=163.336 EndY=163.034 EndZ=0
    g5: LineSegment StartX=163.336 StartY=163.034 StartZ=0 EndX=163.336 EndY=152.034 EndZ=0
    g6: LineSegment StartX=163.336 StartY=152.034 StartZ=0 EndX=142.836 EndY=152.034 EndZ=0
    g7: LineSegment StartX=142.836 StartY=152.034 StartZ=0 EndX=142.836 EndY=163.034 EndZ=0
  constraints (20):
    c: Coincident(g0,g1)
    c: Coincident(g1,g2)
    c: Coincident(g2,g3)
    c: Coincident(g0,g3)
    c: Perpendicular(g0,g3)
    c: Perpendicular(g2,g3)
    c: Perpendicular(g1,g0)
    c: Distance(g0) = 20.5
    c: Distance(g3) = 11
    c: Angle(g2) = 0.994838
    c: Coincident(g4,g5)
    c: Coincident(g5,g6)
    c: Coincident(g6,g7)
    c: Coincident(g7,g4)
    c: Horizontal(g4)
    c: Horizontal(g6)
    c: Vertical(g5)
    c: Vertical(g7)
    c: DistanceY(g5,g5) = 11
    c: DistanceX(g4,g4) = 20.5
FEATURE [PartDesign::Pocket] Pocket013  label="Wall-1"
  Length = 1
  Placement = pos=(0,0,8) rot=(0,0,1;0rad)
  Sketch = -> Sketch049
  Type = 0
FEATURE [Part::Part2DObjectPython] Shape2DView015  label="sDoor-2"  # Draft 2D object (typed FeaturePython)
  Base = -> Pocket012
  HiddenLines = false
  Placement = pos=(2009,978.29,0) rot=(0,0,1;0rad)
  Projection = (-1,0,0)
  ProjectionMode = 0
  SegmentLength = 0.05
  Tessellation = false
FEATURE [Sketcher::SketchObject] Sketch050
  expr: Constraints[9] = Latskap.height
  sketch-geometry (4):
    g0: LineSegment StartX=8 StartY=-200 StartZ=0 EndX=0 EndY=-200 EndZ=0
    g1: LineSegment StartX=0 StartY=-200 StartZ=0 EndX=0 EndY=200 EndZ=0
    g2: LineSegment StartX=0 StartY=200 StartZ=0 EndX=8 EndY=200 EndZ=0
    g3: LineSegment StartX=8 StartY=200 StartZ=0 EndX=8 EndY=-200 EndZ=0
  constraints (12):
    c: Coincident(g0,g1)
    c: Coincident(g1,g2)
    c: Coincident(g2,g3)
    c: Coincident(g3,g0)
    c: Horizontal(g0)
    c: Horizontal(g2)
    c: Vertical(g1)
    c: Vertical(g3)
    c: DistanceX(g2,g2) = 8
    c: DistanceY(g1,g1) = 400
    c: Symmetric(g1,g0,g-1)
    c: DistanceX(g1) = 0
FEATURE [PartDesign::Pad] Pad030  label="Door-outer-1"
  Length = 400
  Length2 = 100
  Sketch = -> Sketch050
  Type = 0
FEATURE [PartDesign::Draft] Draft004  label="Door-outer-draft"
  Angle = 45
  Base = -> Pad030 [Face5,Face1,Face6,Face3]
  NeutralPlane = -> Pad030 [Face2]
  Reversed = true
FEATURE [Sketcher::SketchObject] Sketch051
  Placement = pos=(8,0,0) rot=(0.57735,0.57735,0.57735;2.0944rad)
  Support = -> Draft004 [Face4]
  sketch-geometry (5):
    g0: LineSegment StartX=-39 StartY=274.6 StartZ=0 EndX=39 EndY=274.6 EndZ=0
    g1: LineSegment StartX=39 StartY=274.6 StartZ=0 EndX=39 EndY=134.6 EndZ=0
    g2: LineSegment StartX=39 StartY=134.6 StartZ=0 EndX=-39 EndY=134.6 EndZ=0
    g3: LineSegment StartX=-39 StartY=134.6 StartZ=0 EndX=-39 EndY=274.6 EndZ=0
    g4: LineSegment [constr] StartX=-39 StartY=200 StartZ=0 EndX=39 EndY=200 EndZ=0
  constraints (16):
    c: Coincident(g0,g1)
    c: Coincident(g1,g2)
    c: Coincident(g2,g3)
    c: Coincident(g3,g0)
    c: Horizontal(g0)
    c: Horizontal(g2)
    c: Vertical(g1)
    c: Vertical(g3)
    c: DistanceX(g2,g2) = 78
    c: Symmetric(g2,g1,g-2)
    c: DistanceY(g1,g1) = 140
    c: Horizontal(g4)
    c: PointOnObject(g4,g3)
    c: PointOnObject(g4,g1)
    c: DistanceY(g4) = 200
    c: DistanceY(g2,g4) = 65.4
FEATURE [PartDesign::Pocket] Pocket014  label="Door-outer-pocket"
  Length = 5
  Sketch = -> Sketch051
  Type = 2
FEATURE [Sketcher::SketchObject] Sketch044
  Placement = pos=(8,0,0) rot=(0.57735,0.57735,0.57735;2.0944rad)
  Support = -> Pocket014 [Face2]
  sketch-geometry (20):
    g0: LineSegment StartX=-22 StartY=204 StartZ=0 EndX=-72 EndY=204 EndZ=0
    g1: LineSegment StartX=-72 StartY=204 StartZ=0 EndX=-78.3019 EndY=195 EndZ=0
    g2: ArcOfCircle CenterX=-78.3023 CenterY=163 CenterZ=0 NormalX=0 NormalY=0 NormalZ=1 Radius=32 StartAngle=1.57078 EndAngle=2.78085
    g3: LineSegment StartX=-22 StartY=204 StartZ=0 EndX=-22 EndY=180 EndZ=0
    g4: LineSegment StartX=-22 StartY=180 StartZ=0 EndX=-72 EndY=180 EndZ=0
    g5: LineSegment StartX=-72 StartY=180 StartZ=0 EndX=-78.3019 EndY=189 EndZ=0
    g6: ArcOfCircle CenterX=-78.3023 CenterY=163 CenterZ=0 NormalX=0 NormalY=0 NormalZ=1 Radius=26 StartAngle=1.57078 EndAngle=2.78084
    g7: LineSegment StartX=-108.243 StartY=174.295 StartZ=0 EndX=-166.807 EndY=19.0589 EndZ=0
    g8: LineSegment StartX=-102.629 StartY=172.177 StartZ=0 EndX=-161.193 EndY=16.9411 EndZ=0
    g9: ArcOfCircle CenterX=-164 CenterY=18 CenterZ=0 NormalX=0 NormalY=0 NormalZ=1 Radius=3 StartAngle=2.78084 EndAngle=5.92244
    g10: LineSegment StartX=-22 StartY=204 StartZ=0 EndX=-72 EndY=204 EndZ=0
    g11: LineSegment StartX=-72 StartY=204 StartZ=0 EndX=-74.1006 EndY=207 EndZ=0
    g12: LineSegment StartX=-22 StartY=216 StartZ=0 EndX=-72 EndY=216 EndZ=0
    g13: LineSegment StartX=-74.1006 StartY=213 StartZ=0 EndX=-72 EndY=216 EndZ=0
    g14: LineSegment StartX=-22 StartY=216 StartZ=0 EndX=-22 EndY=204 EndZ=0
    g15: ArcOfCircle CenterX=-76.7263 CenterY=238.867 CenterZ=0 NormalX=0 NormalY=0 NormalZ=1 Radius=26 StartAngle=3.51528 EndAngle=4.81355
    g16: ArcOfCircle CenterX=-76.7263 CenterY=238.867 CenterZ=0 NormalX=0 NormalY=0 NormalZ=1 Radius=31.9751 StartAngle=3.5827 EndAngle=4.7946
    g17: LineSegment StartX=-105.641 StartY=225.216 StartZ=0 EndX=-166.792 EndY=380.903 EndZ=0
    g18: LineSegment StartX=-100.932 StartY=229.376 StartZ=0 EndX=-161.207 EndY=383.095 EndZ=0
    g19: ArcOfCircle CenterX=-164 CenterY=382 CenterZ=0 NormalX=0 NormalY=0 NormalZ=1 Radius=3 StartAngle=0.373687 EndAngle=3.51586
  constraints (61):
    c: Coincident(g0,g1)
    c: Coincident(g1,g2)
    c: Angle(g1,g0) = 2.18166
    c: Horizontal(g0)
    c: Coincident(g5,g6)
    c: Coincident(g4,g5)
    c: Coincident(g3,g4)
    c: Vertical(g3)
    c: Horizontal(g4)
    c: Angle(g4,g5) = 2.18166
    c: Equal(g4,g0)
    c: Equal(g5,g1)
    c: DistanceY(g5,g1) = 6
    c: DistanceY(g3,g3) = 24
    c: DistanceX(g0,g0) = 50
    c: Coincident(g2,g6)
    c: DistanceX(g0) = -22
    c: Parallel(g7,g8)
    c: Coincident(g7,g9)
    c: Coincident(g8,g9)
    c: Tangent(g9,g8)
    c: Tangent(g7,g9)
    c: Radius(g9) = 3
    c: Coincident(g2,g7)
    c: Coincident(g6,g8)
    c: Tangent(g6,g8)
    c: DistanceX(g9) = -164
    c: DistanceY(g9) = 18
    c: Coincident(g10,g11)
    c: Coincident(g12,g14)
    c: Coincident(g10,g14)
    c: Vertical(g14)
    c: DistanceY(g14,g14) = 12
    c: Horizontal(g10)
    c: Horizontal(g12)
    c: Coincident(g12,g13)
    c: Radius(g6) = 26
    c: Coincident(g15,g16)
    c: Coincident(g15,g13)
    c: Coincident(g16,g11)
    c: Angle(g13,g12) = 2.18166
    c: Angle(g10,g11) = 2.18166
    c: DistanceY(g11,g13) = 6
    c: Equal(g10,g12)
    c: Equal(g11,g13)
    c: DistanceX(g12,g12) = 50
    c: Coincident(g17,g19)
    c: Coincident(g18,g19)
    c: Tangent(g19,g18)
    c: Tangent(g19,g17)
    c: Radius(g19) = 3
    c: Coincident(g15,g18)
    c: Coincident(g16,g17)
    c: DistanceX(g19) = -164
    c: DistanceY(g19) = 382
    c: Radius(g15) = 26
    c: DistanceX(g10) = -22
    c: DistanceY(g10) = 204
    c: Coincident(g3,g0)
    c: Tangent(g18,g15)
    c: Coincident(g10,g0)
FEATURE [PartDesign::Pocket] Pocket010  label="Door-Pocket010"
  Length = 5
  Sketch = -> Sketch043
  Type = 2
FEATURE [PartDesign::Pocket] Pocket016  label="Door-0-1"
  Length = 6
  Sketch = -> Sketch044
  Type = 0
FEATURE [Sketcher::SketchObject] Sketch052
  Placement = pos=(8,0,0) rot=(0.57735,0.57735,0.57735;2.0944rad)
  Support = -> Pocket016 [Face2]
  sketch-geometry (40):
    g0: LineSegment [constr] StartX=-182 StartY=340 StartZ=0 EndX=68 EndY=340 EndZ=0
    g1: LineSegment [constr] StartX=68 StartY=340 StartZ=0 EndX=68 EndY=60 EndZ=0
    g2: LineSegment [constr] StartX=68 StartY=60 StartZ=0 EndX=-182 EndY=60 EndZ=0
    g3: LineSegment [constr] StartX=-182 StartY=60 StartZ=0 EndX=-182 EndY=340 EndZ=0
    g4: LineSegment StartX=-62 StartY=68 StartZ=0 EndX=-68.9282 EndY=56 EndZ=0
    g5: LineSegment StartX=-68.9282 StartY=56 StartZ=0 EndX=-55.0718 EndY=56 EndZ=0
    g6: LineSegment StartX=-55.0718 StartY=56 StartZ=0 EndX=-62 EndY=68 EndZ=0
    g7: LineSegment [constr] StartX=-62 StartY=68 StartZ=0 EndX=-62 EndY=60 EndZ=0
    g8: LineSegment [constr] StartX=-68.9282 StartY=56 StartZ=0 EndX=-62 EndY=60 EndZ=0
    g9: LineSegment [constr] StartX=-62 StartY=60 StartZ=0 EndX=-55.0718 EndY=56 EndZ=0
    g10: LineSegment [constr] StartX=-182 StartY=340 StartZ=0 EndX=-182 EndY=348 EndZ=0
    g11: LineSegment [constr] StartX=-182 StartY=340 StartZ=0 EndX=-188.928 EndY=336 EndZ=0
    g12: LineSegment [constr] StartX=-182 StartY=340 StartZ=0 EndX=-175.072 EndY=336 EndZ=0
    g13: LineSegment [constr] StartX=-62 StartY=340 StartZ=0 EndX=-62 EndY=348 EndZ=0
    g14: LineSegment [constr] StartX=-62 StartY=340 StartZ=0 EndX=-68.9282 EndY=336 EndZ=0
    g15: LineSegment [constr] StartX=-62 StartY=340 StartZ=0 EndX=-55.0718 EndY=336 EndZ=0
    g16: LineSegment StartX=-62 StartY=348 StartZ=0 EndX=-68.9282 EndY=336 EndZ=0
    g17: LineSegment StartX=-68.9282 StartY=336 StartZ=0 EndX=-55.0718 EndY=336 EndZ=0
    g18: LineSegment StartX=-55.0718 StartY=336 StartZ=0 EndX=-62 EndY=348 EndZ=0
    g19: LineSegment StartX=-182 StartY=348 StartZ=0 EndX=-188.928 EndY=336 EndZ=0
    g20: LineSegment StartX=-188.928 StartY=336 StartZ=0 EndX=-175.072 EndY=336 EndZ=0
    g21: LineSegment StartX=-175.072 StartY=336 StartZ=0 EndX=-182 EndY=348 EndZ=0
    g22: LineSegment [constr] StartX=68 StartY=340 StartZ=0 EndX=68 EndY=348 EndZ=0
    g23: LineSegment [constr] StartX=68 StartY=340 StartZ=0 EndX=61.0718 EndY=336 EndZ=0
    g24: LineSegment [constr] StartX=68 StartY=340 StartZ=0 EndX=74.9282 EndY=336 EndZ=0
    g25: LineSegment StartX=61.0718 StartY=336 StartZ=0 EndX=74.9282 EndY=336 EndZ=0
    g26: LineSegment StartX=68 StartY=348 StartZ=0 EndX=74.9282 EndY=336 EndZ=0
    g27: LineSegment StartX=68 StartY=348 StartZ=0 EndX=61.0718 EndY=336 EndZ=0
    g28: LineSegment StartX=68 StartY=68 StartZ=0 EndX=61.0718 EndY=56 EndZ=0
    g29: LineSegment StartX=61.0718 StartY=56 StartZ=0 EndX=74.9282 EndY=56 EndZ=0
    g30: LineSegment StartX=74.9282 StartY=56 StartZ=0 EndX=68 EndY=68 EndZ=0
    g31: LineSegment [constr] StartX=68 StartY=60 StartZ=0 EndX=68 EndY=68 EndZ=0
    g32: LineSegment [constr] StartX=61.0718 StartY=56 StartZ=0 EndX=68 EndY=60 EndZ=0
    g33: LineSegment [constr] StartX=74.9282 StartY=56 StartZ=0 EndX=68 EndY=60 EndZ=0
    g34: LineSegment StartX=-182 StartY=68 StartZ=0 EndX=-188.928 EndY=56 EndZ=0
    g35: LineSegment StartX=-188.928 StartY=56 StartZ=0 EndX=-175.072 EndY=56 EndZ=0
    g36: LineSegment StartX=-175.072 StartY=56 StartZ=0 EndX=-182 EndY=68 EndZ=0
    g37: LineSegment [constr] StartX=-182 StartY=60 StartZ=0 EndX=-182 EndY=68 EndZ=0
    g38: LineSegment [constr] StartX=-182 StartY=60 StartZ=0 EndX=-175.072 EndY=56 EndZ=0
    g39: LineSegment [constr] StartX=-182 StartY=60 StartZ=0 EndX=-188.928 EndY=56 EndZ=0
  constraints (104):
    c: Coincident(g0,g1)
    c: Coincident(g1,g2)
    c: Coincident(g2,g3)
    c: Coincident(g3,g0)
    c: Horizontal(g0)
    c: Horizontal(g2)
    c: Vertical(g1)
    c: Vertical(g3)
    c: DistanceY(g1,g1) = 280
    c: DistanceY(g1) = 60
    c: DistanceX(g2,g2) = 250
    c: DistanceX(g2) = -182
    c: Coincident(g4,g5)
    c: Coincident(g5,g6)
    c: Coincident(g6,g4)
    c: Equal(g6,g4)
    c: Equal(g4,g5)
    c: Equal(g8,g7)
    c: Equal(g7,g9)
    c: Coincident(g7,g8)
    c: Coincident(g7,g9)
    c: Coincident(g4,g7)
    c: Coincident(g5,g9)
    c: Coincident(g4,g8)
    c: PointOnObject(g7,g2)
    c: Vertical(g7)
    c: DistanceX(g2,g7) = 120
    c: DistanceY(g4,g7) = 4
    c: Coincident(g0,g10)
    c: Coincident(g0,g11)
    c: Coincident(g0,g12)
    c: Equal(g10,g11)
    c: Equal(g11,g12)
    c: Vertical(g10)
    c: Coincident(g13,g14)
    c: Coincident(g13,g15)
    c: Vertical(g13)
    c: Equal(g14,g13)
    c: Equal(g13,g15)
    c: PointOnObject(g13,g0)
    c: DistanceX(g0,g13) = 120
    c: Coincident(g13,g16)
    c: Coincident(g13,g18)
    c: Coincident(g15,g17)
    c: Coincident(g15,g18)
    c: Coincident(g14,g16)
    c: Coincident(g14,g17)
    c: Equal(g16,g17)
    c: Equal(g17,g18)
    c: DistanceY(g14,g13) = 4
    c: Coincident(g19,g20)
    c: Coincident(g10,g19)
    c: Coincident(g10,g21)
    c: Coincident(g11,g19)
    c: Equal(g21,g19)
    c: Equal(g19,g20)
    c: DistanceY(g11,g0) = 4
    c: Coincident(g22,g26)
    c: Coincident(g22,g27)
    c: Coincident(g23,g25)
    c: Coincident(g23,g27)
    c: Coincident(g24,g25)
    c: Coincident(g24,g26)
    c: Coincident(g0,g22)
    c: Coincident(g0,g23)
    c: Coincident(g0,g24)
    c: Equal(g23,g24)
    c: Equal(g24,g22)
    c: Equal(g27,g26)
    c: Equal(g26,g25)
    c: Vertical(g22)
    c: DistanceY(g23,g0) = 4
    c: Coincident(g28,g29)
    c: Coincident(g29,g30)
    c: Coincident(g28,g30)
    c: Coincident(g1,g31)
    c: Coincident(g1,g32)
    c: Coincident(g1,g33)
    c: Coincident(g28,g31)
    c: Coincident(g28,g32)
    c: Coincident(g29,g33)
    c: Equal(g33,g31)
    c: Equal(g31,g32)
    c: Equal(g30,g29)
    c: Equal(g29,g28)
    c: Vertical(g31)
    c: DistanceY(g28,g1) = 4
    c: Coincident(g21,g20)
    c: Coincident(g12,g20)
    c: Coincident(g34,g35)
    c: Coincident(g35,g36)
    c: Coincident(g36,g34)
    c: Equal(g36,g34)
    c: Equal(g34,g35)
    c: Coincident(g34,g39)
    c: Coincident(g2,g37)
    c: Coincident(g2,g38)
    c: Coincident(g2,g39)
    c: Coincident(g35,g38)
    c: Coincident(g34,g37)
    c: Equal(g37,g39)
    c: Equal(g39,g38)
    c: Vertical(g37)
    c: DistanceY(g34,g2) = 4
FEATURE [PartDesign::Pocket] Pocket017  label="Door"
  Length = 4
  Sketch = -> Sketch052
  Type = 0
FEATURE [Part::Part2DObjectPython] Shape2DView016  label="sDoor-0"  # Draft 2D object (typed FeaturePython)
  Base = -> Pocket017
  HiddenLines = false
  Placement = pos=(1598.49,231,0) rot=(0,0,1;0rad)
  Projection = (1,0,0)
  ProjectionMode = 0
  SegmentLength = 0.05
  Tessellation = false
FEATURE [Part::Feature] Shape2DView017  label="sWall-right-1"
  Placement = pos=(413.493,634,0) rot=(0,1,0;3.14159rad)
  shape: bbox 352 x 384 x 2e-07 mm, 0 faces, 0 solids (baked)
FEATURE [Part::Feature] Shape2DView018  label="sWall-right-3"
  Placement = pos=(786.861,636,0) rot=(0,1,0;3.14159rad)
  shape: bbox 352 x 384 x 2e-07 mm, 0 faces, 0 solids (baked)
FEATURE [Part::Feature] Shape2DView019  label="sWall-right-4"
  Placement = pos=(1601.74,636,0) rot=(0,1,0;3.14159rad)
  shape: bbox 340 x 384 x 2e-07 mm, 0 faces, 0 solids (baked)
FEATURE [Part::Feature] Shape2DView020  label="sWall-right-0"
  Placement = pos=(22.6399,641,0) rot=(0,0,1;0rad)
  shape: bbox 400 x 400 x 2e-07 mm, 0 faces, 0 solids (baked)
FEATURE [Part::Part2DObjectPython] Shape2DView022  label="sRoof"  # Draft 2D object (typed FeaturePython)
  Base = -> Part__Mirroring
  HiddenLines = false
  Placement = pos=(2017.31,31,0) rot=(0,0,1;0rad)
  Projection = (0,1,5.9605e-08)
  ProjectionMode = 0
  SegmentLength = 0.05
  Tessellation = false
FEATURE [Part::Part2DObjectPython] Shape2DView023  label="sBottom"  # Draft 2D object (typed FeaturePython)
  Base = -> Draft002
  HiddenLines = false
  Placement = pos=(2422.77,459,0) rot=(0,0,1;0rad)
  Projection = (0,-1,5.9605e-08)
  ProjectionMode = 0
  SegmentLength = 0.05
  Tessellation = false
FEATURE [Part::Part2DObjectPython] Shape2DView024  label="sRoof-inner"  # Draft 2D object (typed FeaturePython)
  Base = -> Clone005
  HiddenLines = false
  Placement = pos=(1206,815.097,0) rot=(0,0,1;0rad)
  Projection = (0,-1,5.9605e-08)
  ProjectionMode = 0
  SegmentLength = 0.05
  Tessellation = false
FEATURE [Sketcher::SketchObject] Sketch053
  ExternalGeometry = -> [Pad026]
  Placement = pos=(0,-160.1,36) rot=(0,0.707107,0.707107;3.14159rad)
  Support = -> Pad026 [Face1]
  sketch-geometry (31):
    g0: Circle CenterX=-208 CenterY=164 CenterZ=0 NormalX=0 NormalY=0 NormalZ=1 Radius=45
    g1: LineSegment [constr] StartX=-376 StartY=4 StartZ=0 EndX=-40 EndY=4 EndZ=0
    g2: LineSegment [constr] StartX=-376 StartY=324 StartZ=0 EndX=-40 EndY=324 EndZ=0
    g3: Circle CenterX=-318 CenterY=274 CenterZ=0 NormalX=0 NormalY=0 NormalZ=1 Radius=45
    g4: Circle CenterX=-98 CenterY=274 CenterZ=0 NormalX=0 NormalY=0 NormalZ=1 Radius=45
    g5: Circle CenterX=-318 CenterY=54 CenterZ=0 NormalX=0 NormalY=0 NormalZ=1 Radius=45
    g6: Circle CenterX=-318 CenterY=164 CenterZ=0 NormalX=0 NormalY=0 NormalZ=1 Radius=45
    g7: Circle CenterX=-98 CenterY=164 CenterZ=0 NormalX=0 NormalY=0 NormalZ=1 Radius=45
    g8: Circle CenterX=-98 CenterY=54 CenterZ=0 NormalX=0 NormalY=0 NormalZ=1 Radius=45
    g9: LineSegment [constr] StartX=-318 StartY=274 StartZ=0 EndX=-98 EndY=274 EndZ=0
    g10: LineSegment [constr] StartX=-98 StartY=274 StartZ=0 EndX=-98 EndY=54 EndZ=0
    g11: LineSegment [constr] StartX=-98 StartY=54 StartZ=0 EndX=-318 EndY=54 EndZ=0
    g12: LineSegment [constr] StartX=-318 StartY=54 StartZ=0 EndX=-318 EndY=274 EndZ=0
    g13: Circle CenterX=-208 CenterY=274 CenterZ=0 NormalX=0 NormalY=0 NormalZ=1 Radius=45
    g14: Circle CenterX=-208 CenterY=54 CenterZ=0 NormalX=0 NormalY=0 NormalZ=1 Radius=45
    g15: LineSegment [constr] StartX=-318 StartY=164 StartZ=0 EndX=-98 EndY=274 EndZ=0
    g16: LineSegment [constr] StartX=-318 StartY=164 StartZ=0 EndX=-98 EndY=54 EndZ=0
    g17: LineSegment [constr] StartX=-98 StartY=164 StartZ=0 EndX=-318 EndY=274 EndZ=0
    g18: LineSegment [constr] StartX=-318 StartY=54 StartZ=0 EndX=-98 EndY=164 EndZ=0
    g19: LineSegment [constr] StartX=-208 StartY=54 StartZ=0 EndX=-98 EndY=274 EndZ=0
    g20: LineSegment [constr] StartX=-318 StartY=54 StartZ=0 EndX=-208 EndY=274 EndZ=0
    g21: LineSegment [constr] StartX=-208 StartY=274 StartZ=0 EndX=-98 EndY=54 EndZ=0
    g22: LineSegment [constr] StartX=-208 StartY=164 StartZ=0 EndX=-98 EndY=54 EndZ=0
    g23: LineSegment [constr] StartX=-208 StartY=164 StartZ=0 EndX=-98 EndY=274 EndZ=0
    g24: LineSegment [constr] StartX=-208 StartY=164 StartZ=0 EndX=-318 EndY=54 EndZ=0
    g25: LineSegment [constr] StartX=-318 StartY=274 StartZ=0 EndX=-208 EndY=54 EndZ=0
    g26: LineSegment [constr] StartX=-376 StartY=324 StartZ=0 EndX=-208 EndY=164 EndZ=0
    g27: LineSegment [constr] StartX=-208 StartY=164 StartZ=0 EndX=-40 EndY=324 EndZ=0
    g28: Circle CenterX=-147.1 CenterY=164 CenterZ=0 NormalX=0 NormalY=0 NormalZ=1 Radius=1.7
    g29: Circle CenterX=-157.1 CenterY=164 CenterZ=0 NormalX=0 NormalY=0 NormalZ=1 Radius=1.7
    g30: LineSegment [constr] StartX=-147.1 StartY=164 StartZ=0 EndX=-157.1 EndY=164 EndZ=0
  constraints (77):
    c: PointOnObject(g1,g-3)
    c: Horizontal(g1)
    c: DistanceY(g-3,g1) = 4
    c: PointOnObject(g2,g-3)
    c: Horizontal(g2)
    c: DistanceY(g2,g-3) = 4
    c: Radius(g0) = 45
    c: Coincident(g9,g10)
    c: Coincident(g10,g11)
    c: Coincident(g11,g12)
    c: Coincident(g12,g9)
    c: Horizontal(g9)
    c: Horizontal(g11)
    c: Vertical(g10)
    c: Vertical(g12)
    c: Coincident(g9,g3)
    c: Coincident(g10,g8)
    c: Coincident(g4,g9)
    c: Coincident(g5,g11)
    c: PointOnObject(g6,g12)
    c: PointOnObject(g7,g10)
    c: PointOnObject(g13,g9)
    c: PointOnObject(g14,g11)
    c: Equal(g3,g13)
    c: Equal(g13,g4)
    c: Equal(g4,g7)
    c: Equal(g7,g8)
    c: Equal(g8,g14)
    c: Equal(g14,g5)
    c: Equal(g5,g6)
    c: Equal(g6,g0)
    c: Coincident(g15,g6)
    c: Coincident(g15,g4)
    c: Coincident(g16,g8)
    c: Coincident(g17,g3)
    c: Coincident(g18,g5)
    c: Coincident(g7,g17)
    c: Coincident(g7,g18)
    c: Equal(g18,g17)
    c: Coincident(g6,g16)
    c: Equal(g15,g16)
    c: Coincident(g19,g14)
    c: Coincident(g19,g4)
    c: Coincident(g20,g5)
    c: Coincident(g20,g13)
    c: Coincident(g21,g8)
    c: Equal(g21,g20)
    c: Coincident(g13,g21)
    c: Coincident(g22,g8)
    c: Coincident(g23,g4)
    c: Equal(g23,g22)
    c: Coincident(g24,g5)
    c: Equal(g24,g22)
    c: DistanceY(g0) = 164
    c: Coincident(g25,g3)
    c: Coincident(g25,g14)
    c: Equal(g25,g19)
    c: Coincident(g0,g22)
    c: Coincident(g0,g23)
    c: Coincident(g0,g24)
    c: Coincident(g0,g26)
    c: Coincident(g0,g27)
    c: Equal(g27,g26)
    c: DistanceX(g1,g1) = 336
    c: DistanceX(g2,g2) = 336
    c: Coincident(g26,g2)
    c: Coincident(g27,g2)
    c: Equal(g9,g10)
    c: DistanceX(g9,g9) = 220
    c: Coincident(g30,g28)
    c: Horizontal(g30)
    c: Coincident(g29,g30)
    c: Equal(g28,g29)
    c: Radius(g29) = 1.7
    c: DistanceY(g28) = 164
    c: DistanceX(g30,g30) = 10
    c: DistanceX(g28) = -147.1
FEATURE [PartDesign::Pocket] Pocket018  label="Floor-inner"
  Length = 5
  Placement = pos=(0,0,36) rot=(0,0,1;0rad)
  Sketch = -> Sketch053
  Type = 2
FEATURE [Part::Part2DObjectPython] Rectangle001  label="Aluminium"  # Draft 2D object (typed FeaturePython)
  ChamferSize = 0
  Columns = 1
  FilletRadius = 0
  Height = 301
  Length = 859
  MakeFace = false
  Placement = pos=(8,1268,0) rot=(0,0,1;0rad)
  Rows = 1
FEATURE [Part::Part2DObjectPython] Shape2DView026  label="aluUpper-left"  # Draft 2D object (typed FeaturePython)
  Base = -> Pad010
  HiddenLines = false
  Placement = pos=(151.496,1606.79,0) rot=(0,0,-1;0.994838rad)
  Projection = (0,0,1)
  ProjectionMode = 0
  SegmentLength = 0.05
  Tessellation = false
FEATURE [Part::Part2DObjectPython] Shape2DView027  label="aluLower-left"  # Draft 2D object (typed FeaturePython)
  Base = -> Pad009
  HiddenLines = false
  Placement = pos=(141.591,1531.19,0) rot=(0,0,-1;0.994838rad)
  Projection = (0,0,1)
  ProjectionMode = 0
  SegmentLength = 0.05
  Tessellation = false
FEATURE [Part::Feature] Shape2DView028  label="aluLower-right"
  Placement = pos=(158.324,1564.88,0) rot=(0,0,-1;0.994838rad)
  shape: bbox 414.7 x 159.6 x 2e-07 mm, 0 faces, 0 solids (baked)
FEATURE [Part::Feature] Shape2DView029  label="aluUpper-right"
  Placement = pos=(139.877,1577.02,0) rot=(0,0,-1;0.994838rad)
  shape: bbox 414.7 x 159.6 x 2e-07 mm, 0 faces, 0 solids (baked)
FEATURE [Part::Feature] Shape2DView030  label="sWall-2-right"
  Placement = pos=(281,830.255,0) rot=(0,0,1;1.5708rad)
  shape: bbox 384 x 352 x 2e-07 mm, 0 faces, 0 solids (baked)
FEATURE [Part::Part2DObjectPython] Shape2DView031  label="sFront"  # Draft 2D object (typed FeaturePython)
  Base = -> Pad024
  FaceNumbers = [17]
  HiddenLines = false
  Placement = pos=(421.807,1035.05,0) rot=(0,0,1;0rad)
  Projection = (1,0,0)
  ProjectionMode = 0
  SegmentLength = 0.05
  Tessellation = false
FEATURE [Sketcher::SketchObject] Sketch054
  Placement = pos=(400,0,0) rot=(0.57735,0.57735,0.57735;2.0944rad)
  Support = -> Pad011 [Face25]
  sketch-geometry (29):
    g0: LineSegment [constr] StartX=-182 StartY=330 StartZ=0 EndX=182 EndY=330 EndZ=0
    g1: LineSegment [constr] StartX=182 StartY=330 StartZ=0 EndX=182 EndY=70 EndZ=0
    g2: LineSegment [constr] StartX=182 StartY=70 StartZ=0 EndX=-182 EndY=70 EndZ=0
    g3: LineSegment [constr] StartX=-182 StartY=70 StartZ=0 EndX=-182 EndY=330 EndZ=0
    g4: LineSegment [constr] StartX=-182 StartY=200 StartZ=0 EndX=182 EndY=200 EndZ=0
    g5: LineSegment [constr] StartX=-182 StartY=330 StartZ=0 EndX=-172 EndY=330 EndZ=0
    g6: LineSegment [constr] StartX=-182 StartY=330 StartZ=0 EndX=-187 EndY=321.34 EndZ=0
    g7: LineSegment [constr] StartX=-182 StartY=330 StartZ=0 EndX=-187 EndY=338.66 EndZ=0
    g8: LineSegment StartX=-187 StartY=338.66 StartZ=0 EndX=-172 EndY=330 EndZ=0
    g9: LineSegment StartX=-172 StartY=330 StartZ=0 EndX=-187 EndY=321.34 EndZ=0
    g10: LineSegment StartX=-187 StartY=321.34 StartZ=0 EndX=-187 EndY=338.66 EndZ=0
    g11: LineSegment StartX=-172 StartY=70 StartZ=0 EndX=-187 EndY=78.6603 EndZ=0
    g12: LineSegment StartX=-187 StartY=78.6603 StartZ=0 EndX=-187 EndY=61.3397 EndZ=0
    g13: LineSegment StartX=-187 StartY=61.3397 StartZ=0 EndX=-172 EndY=70 EndZ=0
    g14: LineSegment [constr] StartX=-182 StartY=70 StartZ=0 EndX=-187 EndY=78.6603 EndZ=0
    g15: LineSegment [constr] StartX=-182 StartY=70 StartZ=0 EndX=-187 EndY=61.3397 EndZ=0
    g16: LineSegment [constr] StartX=-182 StartY=70 StartZ=0 EndX=-172 EndY=70 EndZ=0
    g17: LineSegment [constr] StartX=182 StartY=70 StartZ=0 EndX=192 EndY=70 EndZ=0
    g18: LineSegment [constr] StartX=182 StartY=70 StartZ=0 EndX=177 EndY=78.6603 EndZ=0
    g19: LineSegment [constr] StartX=182 StartY=70 StartZ=0 EndX=177 EndY=61.3397 EndZ=0
    g20: LineSegment StartX=177 StartY=78.6603 StartZ=0 EndX=177 EndY=61.3397 EndZ=0
    g21: LineSegment StartX=177 StartY=61.3397 StartZ=0 EndX=192 EndY=70 EndZ=0
    g22: LineSegment StartX=192 StartY=70 StartZ=0 EndX=177 EndY=78.6603 EndZ=0
    g23: LineSegment StartX=192 StartY=330 StartZ=0 EndX=177 EndY=338.66 EndZ=0
    g24: LineSegment StartX=177 StartY=338.66 StartZ=0 EndX=177 EndY=321.34 EndZ=0
    g25: LineSegment StartX=177 StartY=321.34 StartZ=0 EndX=192 EndY=330 EndZ=0
    g26: LineSegment [constr] StartX=182 StartY=330 StartZ=0 EndX=192 EndY=330 EndZ=0
    g27: LineSegment [constr] StartX=182 StartY=330 StartZ=0 EndX=177 EndY=338.66 EndZ=0
    g28: LineSegment [constr] StartX=177 StartY=321.34 StartZ=0 EndX=182 EndY=330 EndZ=0
  constraints (76):
    c: Coincident(g0,g1)
    c: Coincident(g1,g2)
    c: Coincident(g2,g3)
    c: Coincident(g3,g0)
    c: Horizontal(g0)
    c: Horizontal(g2)
    c: Vertical(g1)
    c: Vertical(g3)
    c: Horizontal(g4)
    c: Symmetric(g0,g1,g4)
    c: PointOnObject(g4,g1)
    c: PointOnObject(g4,g3)
    c: DistanceY(g1,g1) = 260
    c: Symmetric(g2,g1,g-2)
    c: DistanceY(g4) = 200
    c: DistanceX(g2) = -182
    c: Coincident(g5,g0)
    c: Coincident(g6,g0)
    c: Equal(g6,g7)
    c: Equal(g7,g5)
    c: Coincident(g8,g9)
    c: Coincident(g9,g10)
    c: Coincident(g7,g8)
    c: Coincident(g7,g10)
    c: Coincident(g6,g9)
    c: Coincident(g5,g8)
    c: Equal(g8,g9)
    c: Equal(g9,g10)
    c: Coincident(g0,g7)
    c: Horizontal(g5)
    c: DistanceX(g7,g0) = 5
    c: Coincident(g11,g12)
    c: Coincident(g12,g13)
    c: Coincident(g11,g13)
    c: Coincident(g11,g16)
    c: Coincident(g11,g14)
    c: Coincident(g2,g14)
    c: Coincident(g2,g15)
    c: Coincident(g2,g16)
    c: Coincident(g12,g15)
    c: Equal(g15,g14)
    c: Equal(g14,g16)
    c: Equal(g13,g11)
    c: Equal(g11,g12)
    c: Horizontal(g16)
    c: DistanceX(g12,g2) = 5
    c: Coincident(g20,g21)
    c: Coincident(g21,g22)
    c: Coincident(g18,g20)
    c: Coincident(g18,g22)
    c: Coincident(g19,g20)
    c: Coincident(g1,g17)
    c: Coincident(g1,g18)
    c: Coincident(g1,g19)
    c: Coincident(g17,g21)
    c: Equal(g17,g18)
    c: Equal(g18,g19)
    c: Equal(g22,g21)
    c: Equal(g21,g20)
    c: Horizontal(g17)
    c: DistanceX(g18,g1) = 5
    c: Coincident(g23,g24)
    c: Coincident(g24,g25)
    c: Coincident(g23,g25)
    c: Coincident(g0,g26)
    c: Coincident(g0,g27)
    c: Coincident(g0,g28)
    c: Coincident(g23,g26)
    c: Coincident(g23,g27)
    c: Coincident(g24,g28)
    c: Equal(g25,g24)
    c: Equal(g24,g23)
    c: Equal(g26,g28)
    c: Equal(g28,g27)
    c: Horizontal(g26)
    c: DistanceX(g23,g0) = 5
FEATURE [PartDesign::Pocket] Pocket019  label="Back-pocket"
  Length = 4
  Placement = pos=(400,0,0) rot=(0.57735,0.57735,0.57735;2.0944rad)
  Sketch = -> Sketch054
  Type = 0
FEATURE [Sketcher::SketchObject] Sketch055
  Placement = pos=(384,0,0) rot=(0.57735,0.57735,0.57735;2.0944rad)
  sketch-geometry (17):
    g0: LineSegment StartX=-192 StartY=340 StartZ=0 EndX=192 EndY=340 EndZ=0
    g1: LineSegment StartX=192 StartY=340 StartZ=0 EndX=192 EndY=320 EndZ=0
    g2: LineSegment StartX=192 StartY=320 StartZ=0 EndX=-192 EndY=320 EndZ=0
    g3: LineSegment StartX=-192 StartY=320 StartZ=0 EndX=-192 EndY=340 EndZ=0
    g4: LineSegment StartX=-192 StartY=80 StartZ=0 EndX=192 EndY=80 EndZ=0
    g5: LineSegment StartX=192 StartY=60 StartZ=0 EndX=-192 EndY=60 EndZ=0
    g6: LineSegment StartX=-192 StartY=60 StartZ=0 EndX=-192 EndY=80 EndZ=0
    g7: LineSegment StartX=192 StartY=80 StartZ=0 EndX=192 EndY=60 EndZ=0
    g8: LineSegment [constr] StartX=-200 StartY=200 StartZ=0 EndX=200 EndY=200 EndZ=0
    g9: Circle CenterX=182 CenterY=70 CenterZ=0 NormalX=0 NormalY=0 NormalZ=1 Radius=3
    g10: LineSegment [constr] StartX=182 StartY=70 StartZ=0 EndX=-182 EndY=70 EndZ=0
    g11: LineSegment [constr] StartX=-182 StartY=70 StartZ=0 EndX=-182 EndY=330 EndZ=0
    g12: LineSegment [constr] StartX=-182 StartY=330 StartZ=0 EndX=182 EndY=330 EndZ=0
    g13: LineSegment [constr] StartX=182 StartY=330 StartZ=0 EndX=182 EndY=70 EndZ=0
    g14: Circle CenterX=-182 CenterY=70 CenterZ=0 NormalX=0 NormalY=0 NormalZ=1 Radius=3
    g15: Circle CenterX=-182 CenterY=330 CenterZ=0 NormalX=0 NormalY=0 NormalZ=1 Radius=3
    g16: Circle CenterX=182 CenterY=330 CenterZ=0 NormalX=0 NormalY=0 NormalZ=1 Radius=3
  constraints (47):
    c: Coincident(g0,g1)
    c: Coincident(g1,g2)
    c: Coincident(g2,g3)
    c: Coincident(g3,g0)
    c: Horizontal(g0)
    c: Horizontal(g2)
    c: Vertical(g1)
    c: Vertical(g3)
    c: Coincident(g5,g6)
    c: Coincident(g6,g4)
    c: Horizontal(g4)
    c: Horizontal(g5)
    c: Vertical(g6)
    c: Equal(g5,g2)
    c: DistanceY(g1,g1) = 20
    c: Equal(g1,g6)
    c: Coincident(g7,g4)
    c: Coincident(g7,g5)
    c: Vertical(g7)
    c: DistanceX(g5,g5) = 384
    c: Symmetric(g1,g2,g-2)
    c: Symmetric(g5,g5,g-2)
    c: DistanceY(g8) = 200
    c: Symmetric(g1,g4,g8)
    c: DistanceY(g5) = 60
    c: Coincident(g10,g11)
    c: Coincident(g11,g12)
    c: Coincident(g12,g13)
    c: Coincident(g13,g10)
    c: Horizontal(g10)
    c: Horizontal(g12)
    c: Vertical(g11)
    c: Vertical(g13)
    c: Coincident(g9,g10)
    c: DistanceY(g-1,g9) = 70
    c: Coincident(g14,g10)
    c: Symmetric(g10,g9,g-2)
    c: Coincident(g15,g11)
    c: Coincident(g16,g12)
    c: Symmetric(g12,g9,g8)
    c: DistanceX(g8) = 200
    c: DistanceX(g8) = -200
    c: DistanceX(g12) = 182
    c: Radius(g16) = 3
    c: Equal(g14,g15)
    c: Equal(g15,g16)
    c: Equal(g16,g9)
FEATURE [PartDesign::Pad] Pad031  label="Back-1"
  Length = 8
  Length2 = 100
  Placement = pos=(384,0,0) rot=(0.57735,0.57735,0.57735;2.0944rad)
  Sketch = -> Sketch055
  Type = 0
FEATURE [PartDesign::Draft] Draft005  label="Back"
  Angle = 45
  Base = -> Pocket019 [Face2,Face1,Face3,Face6]
  NeutralPlane = -> Pocket019 [Face4]
  Placement = pos=(400,0,0) rot=(0.57735,0.57735,0.57735;2.0944rad)
FEATURE [App::DocumentObjectGroup] Group004  label="Outer"
  Group = -> [Part__Mirroring001,Part__Mirroring,Pocket017,Draft005,All]
FEATURE [Sketcher::SketchObject] Sketch056
  ExternalGeometry = -> [Pad025]
  Placement = pos=(376,0,400) rot=(-0.57735,-0.57735,0.57735;2.0944rad)
  Support = -> Pad025 [Face18]
  sketch-geometry (17):
    g0: LineSegment StartX=-168.2 StartY=360 StartZ=0 EndX=-160.1 EndY=360 EndZ=0
    g1: LineSegment StartX=-160.1 StartY=360 StartZ=0 EndX=-160.1 EndY=40 EndZ=0
    g2: LineSegment StartX=-160.1 StartY=40 StartZ=0 EndX=-168.2 EndY=40 EndZ=0
    g3: LineSegment StartX=-168.2 StartY=40 StartZ=0 EndX=-168.2 EndY=360 EndZ=0
    g4: LineSegment StartX=160.1 StartY=360 StartZ=0 EndX=168.2 EndY=360 EndZ=0
    g5: LineSegment StartX=168.2 StartY=360 StartZ=0 EndX=168.2 EndY=40 EndZ=0
    g6: LineSegment StartX=168.2 StartY=40 StartZ=0 EndX=160.1 EndY=40 EndZ=0
    g7: LineSegment StartX=160.1 StartY=40 StartZ=0 EndX=160.1 EndY=360 EndZ=0
    g8: LineSegment [constr] StartX=-182 StartY=330 StartZ=0 EndX=182 EndY=330 EndZ=0
    g9: LineSegment [constr] StartX=182 StartY=330 StartZ=0 EndX=182 EndY=70 EndZ=0
    g10: LineSegment [constr] StartX=182 StartY=70 StartZ=0 EndX=-182 EndY=70 EndZ=0
    g11: LineSegment [constr] StartX=-182 StartY=70 StartZ=0 EndX=-182 EndY=330 EndZ=0
    g12: Circle CenterX=-182 CenterY=330 CenterZ=0 NormalX=0 NormalY=0 NormalZ=1 Radius=10
    g13: Circle CenterX=182 CenterY=330 CenterZ=0 NormalX=0 NormalY=0 NormalZ=1 Radius=10
    g14: Circle CenterX=182 CenterY=70 CenterZ=0 NormalX=0 NormalY=0 NormalZ=1 Radius=10
    g15: Circle CenterX=-182 CenterY=70 CenterZ=0 NormalX=0 NormalY=0 NormalZ=1 Radius=10
    g16: LineSegment [constr] StartX=-200 StartY=200 StartZ=0 EndX=200 EndY=200 EndZ=0
  constraints (47):
    c: Coincident(g0,g1)
    c: Coincident(g1,g2)
    c: Coincident(g2,g3)
    c: Coincident(g3,g0)
    c: Horizontal(g0)
    c: Horizontal(g2)
    c: Vertical(g1)
    c: Vertical(g3)
    c: DistanceX(g0,g0) = 8.1
    c: DistanceY(g3,g3) = 320
    c: Coincident(g4,g5)
    c: Coincident(g5,g6)
    c: Coincident(g6,g7)
    c: Coincident(g7,g4)
    c: Horizontal(g4)
    c: Horizontal(g6)
    c: Vertical(g5)
    c: Vertical(g7)
    c: DistanceX(g4,g4) = 8.1
    c: DistanceY(g5,g5) = 320
    c: Coincident(g8,g9)
    c: Coincident(g9,g10)
    c: Coincident(g10,g11)
    c: Coincident(g11,g8)
    c: Horizontal(g8)
    c: Horizontal(g10)
    c: Vertical(g9)
    c: Vertical(g11)
    c: Coincident(g12,g8)
    c: Coincident(g13,g8)
    c: Coincident(g14,g9)
    c: Coincident(g15,g10)
    c: Equal(g15,g12)
    c: Equal(g12,g13)
    c: Equal(g13,g14)
    c: Radius(g13) = 10
    c: Symmetric(g10,g9,g-2)
    c: DistanceX(g-1,g8) = 182
    c: Horizontal(g16)
    c: Symmetric(g16,g16,g-2)
    c: DistanceX(g16) = 200
    c: DistanceY(g16) = 200
    c: Symmetric(g8,g9,g16)
    c: DistanceY(g9) = 70
    c: DistanceY(g-1,g5) = 40
    c: Symmetric(g5,g2,g-2)
    c: DistanceX(g1) = -160.1
FEATURE [PartDesign::Pocket] Pocket020  label="Back-2"
  Length = 4.1
  Placement = pos=(384,0,400) rot=(0.57735,0.57735,0.57735;2.0944rad)
  Sketch = -> Sketch056
  Type = 0
FEATURE [Sketcher::SketchObject] Sketch057
  Placement = pos=(0,-168,0) rot=(1,0,0;1.5708rad)
  sketch-geometry (4):
    g0: Circle CenterX=98 CenterY=200 CenterZ=0 NormalX=0 NormalY=0 NormalZ=1 Radius=45
    g1: Circle CenterX=103 CenterY=200 CenterZ=0 NormalX=0 NormalY=0 NormalZ=1 Radius=1.7
    g2: Circle CenterX=93 CenterY=200 CenterZ=0 NormalX=0 NormalY=0 NormalZ=1 Radius=1.7
    g3: LineSegment [constr] StartX=93 StartY=200 StartZ=0 EndX=103 EndY=200 EndZ=0
  constraints (11):
    c: Radius(g0) = 45
    c: Coincident(g3,g1)
    c: Horizontal(g3)
    c: Coincident(g2,g3)
    c: PointOnObject(g0,g3)
    c: DistanceX(g0,g1) = 5
    c: DistanceX(g2,g0) = 5
    c: Equal(g2,g1)
    c: Radius(g1) = 1.7
    c: DistanceY(g0) = 200
    c: DistanceX(g0) = 98
FEATURE [PartDesign::Pad] Pad032  label="Weight-holder"
  Length = 8
  Length2 = 100
  Placement = pos=(0,-168,0) rot=(1,0,0;1.5708rad)
  Reversed = true
  Sketch = -> Sketch057
  Type = 0
FEATURE [Sketcher::SketchObject] Sketch058
  Placement = pos=(87.5,-180,200) rot=(0.57735,0.57735,0.57735;2.0944rad)
  sketch-geometry (4):
    g0: LineSegment StartX=-6.3 StartY=6.3 StartZ=0 EndX=6.3 EndY=6.3 EndZ=0
    g1: LineSegment StartX=6.3 StartY=6.3 StartZ=0 EndX=6.3 EndY=-6.3 EndZ=0
    g2: LineSegment StartX=6.3 StartY=-6.3 StartZ=0 EndX=-6.3 EndY=-6.3 EndZ=0
    g3: LineSegment StartX=-6.3 StartY=-6.3 StartZ=0 EndX=-6.3 EndY=6.3 EndZ=0
  constraints (12):
    c: Coincident(g0,g1)
    c: Coincident(g1,g2)
    c: Coincident(g2,g3)
    c: Coincident(g3,g0)
    c: Horizontal(g0)
    c: Horizontal(g2)
    c: Vertical(g1)
    c: Vertical(g3)
    c: Symmetric(g0,g0,g-2)
    c: Symmetric(g0,g1,g-1)
    c: Equal(g0,g1)
    c: DistanceY(g1,g1) = 12.6
FEATURE [PartDesign::Pad] Pad033  label="Weight-cell-1"
  Length = 75
  Length2 = 100
  Placement = pos=(87.5,-180,200) rot=(0.57735,0.57735,0.57735;2.0944rad)
  Sketch = -> Sketch058
  Type = 0
FEATURE [App::DocumentObjectGroup] Group002  label="Unused"
  Group = -> [Pad002,Pad014,Pad017,Pad018,Pad004,Pocket,Pad011,Pad008,MultiTransform,Pocket002,Pad019,Pad,Pad020,Pad013,Revolution,Pocket004,Pad015,Draft003,Pocket010,Pad029,Draft004,Pocket014,Pad030,Pocket016,Pocket019,Pad026,Pad033,Pad025]
FEATURE [Sketcher::SketchObject] Sketch059
  Placement = pos=(87.5,-186.3,200) rot=(0.57735,0.57735,-0.57735;2.0944rad)
  Support = -> Pad033 [Face4]
  expr: Constraints[11] = 68 + 3.2 / 2
  expr: Constraints[1] = 3.8 + 3.2 / 2
  sketch-geometry (4):
    g0: Circle CenterX=0 CenterY=5.4 CenterZ=0 NormalX=0 NormalY=0 NormalZ=1 Radius=1.5
    g1: Circle CenterX=0 CenterY=15.4 CenterZ=0 NormalX=0 NormalY=0 NormalZ=1 Radius=1.5
    g2: Circle CenterX=0 CenterY=69.6 CenterZ=0 NormalX=0 NormalY=0 NormalZ=1 Radius=1.5
    g3: Circle CenterX=0 CenterY=59.6 CenterZ=0 NormalX=0 NormalY=0 NormalZ=1 Radius=1.5
  constraints (12):
    c: PointOnObject(g0,g-2)
    c: DistanceY(g0) = 5.4
    c: PointOnObject(g1,g-2)
    c: DistanceY(g0,g1) = 10
    c: Equal(g0,g1)
    c: Radius(g1) = 1.5
    c: PointOnObject(g3,g-2)
    c: PointOnObject(g2,g-2)
    c: DistanceY(g3,g2) = 10
    c: Equal(g2,g3)
    c: Radius(g2) = 1.5
    c: DistanceY(g2) = 69.6
FEATURE [PartDesign::Pocket] Pocket021  label="Weight-cell"
  Length = 5
  Placement = pos=(87.5,-180,200) rot=(0.57735,0.57735,0.57735;2.0944rad)
  Sketch = -> Sketch059
  Type = 2
FEATURE [Part::Part2DObjectPython] Shape2DView032  label="sWeight"  # Draft 2D object (typed FeaturePython)
  Base = -> Pad032
  FaceNumbers = [4]
  HiddenLines = false
  Placement = pos=(-20,1407,0) rot=(0,0,1;0rad)
  Projection = (0,1,5.9605e-08)
  ProjectionMode = 0
  SegmentLength = 0.05
  Tessellation = false
FEATURE [Part::Part2DObjectPython] Shape2DView033  label="sFloor-inner"  # Draft 2D object (typed FeaturePython)
  Base = -> Pocket018
  FaceNumbers = [0]
  HiddenLines = false
  Placement = pos=(1200,830,0) rot=(0,0,1;0rad)
  Projection = (0,1,5.9605e-08)
  ProjectionMode = 0
  SegmentLength = 0.05
  Tessellation = false
FEATURE [Part::Part2DObjectPython] Rectangle002  label="Acrylic-5mm"  # Draft 2D object (typed FeaturePython)
  ChamferSize = 0
  Columns = 1
  FilletRadius = 0
  Height = 300
  Length = 400
  MakeFace = false
  Placement = pos=(915,1268,0) rot=(0,0,1;0rad)
  Rows = 1
FEATURE [Part::Part2DObjectPython] Shape2DView034  label="sBig-gear"  # Draft 2D object (typed FeaturePython)
  Base = -> Pocket006
  HiddenLines = false
  Placement = pos=(666,1390,0) rot=(0,0,1;0rad)
  Projection = (0,0,1)
  ProjectionMode = 0
  SegmentLength = 0.05
  Tessellation = false
FEATURE [Part::Part2DObjectPython] Clone2D002  label="sBig-gear-right"  # Draft 2D object (typed FeaturePython)
  Objects = -> [Shape2DView034]
  Placement = pos=(1439,1390,0) rot=(0,1,0;3.14159rad)
  Scale = (1,1,1)
FEATURE [Part::Mirroring] Part__Mirroring004  label="Wall-inner (Mirror #5)"
  Base = (0,0,200)
  Normal = (0,0,1)
  Source = -> Pocket009
FEATURE [Part::Mirroring] Part__Mirroring005  label="Wall-1 (Mirror #6)"
  Base = (0,0,196)
  Normal = (0,0,1)
  Source = -> Pocket013
FEATURE [Sketcher::SketchObject] Sketch062
  Placement = pos=(0,-160.1,36) rot=(0,0.707107,0.707107;3.14159rad)
  sketch-geometry (25):
    g0: Circle CenterX=-208 CenterY=164 CenterZ=0 NormalX=0 NormalY=0 NormalZ=1 Radius=45
    g1: LineSegment [constr] StartX=-376 StartY=4 StartZ=0 EndX=-40 EndY=4 EndZ=0
    g2: LineSegment [constr] StartX=-376 StartY=324 StartZ=0 EndX=-40 EndY=324 EndZ=0
    g3: Circle CenterX=-318 CenterY=274 CenterZ=0 NormalX=0 NormalY=0 NormalZ=1 Radius=45
    g4: Circle CenterX=-98 CenterY=274 CenterZ=0 NormalX=0 NormalY=0 NormalZ=1 Radius=45
    g5: Circle CenterX=-318 CenterY=54 CenterZ=0 NormalX=0 NormalY=0 NormalZ=1 Radius=45
    g6: Circle CenterX=-318 CenterY=164 CenterZ=0 NormalX=0 NormalY=0 NormalZ=1 Radius=45
    g7: Circle CenterX=-98 CenterY=54 CenterZ=0 NormalX=0 NormalY=0 NormalZ=1 Radius=45
    g8: LineSegment [constr] StartX=-318 StartY=274 StartZ=0 EndX=-98 EndY=274 EndZ=0
    g9: LineSegment [constr] StartX=-98 StartY=274 StartZ=0 EndX=-98 EndY=54 EndZ=0
    g10: LineSegment [constr] StartX=-98 StartY=54 StartZ=0 EndX=-318 EndY=54 EndZ=0
    g11: LineSegment [constr] StartX=-318 StartY=54 StartZ=0 EndX=-318 EndY=274 EndZ=0
    g12: Circle CenterX=-208 CenterY=274 CenterZ=0 NormalX=0 NormalY=0 NormalZ=1 Radius=45
    g13: Circle CenterX=-208 CenterY=54 CenterZ=0 NormalX=0 NormalY=0 NormalZ=1 Radius=45
    g14: LineSegment [constr] StartX=-318 StartY=164 StartZ=0 EndX=-98 EndY=274 EndZ=0
    g15: LineSegment [constr] StartX=-318 StartY=164 StartZ=0 EndX=-98 EndY=54 EndZ=0
    g16: LineSegment [constr] StartX=-208 StartY=54 StartZ=0 EndX=-98 EndY=274 EndZ=0
    g17: LineSegment [constr] StartX=-318 StartY=54 StartZ=0 EndX=-208 EndY=274 EndZ=0
    g18: LineSegment [constr] StartX=-208 StartY=274 StartZ=0 EndX=-98 EndY=54 EndZ=0
    g19: LineSegment [constr] StartX=-208 StartY=164 StartZ=0 EndX=-98 EndY=54 EndZ=0
    g20: LineSegment [constr] StartX=-208 StartY=164 StartZ=0 EndX=-98 EndY=274 EndZ=0
    g21: LineSegment [constr] StartX=-208 StartY=164 StartZ=0 EndX=-318 EndY=54 EndZ=0
    g22: LineSegment [constr] StartX=-318 StartY=274 StartZ=0 EndX=-208 EndY=54 EndZ=0
    g23: LineSegment [constr] StartX=-376 StartY=324 StartZ=0 EndX=-208 EndY=164 EndZ=0
    g24: LineSegment [constr] StartX=-208 StartY=164 StartZ=0 EndX=-40 EndY=324 EndZ=0
  constraints (57):
    c: Horizontal(g1)
    c: Horizontal(g2)
    c: Radius(g0) = 45
    c: Coincident(g8,g9)
    c: Coincident(g9,g10)
    c: Coincident(g10,g11)
    c: Coincident(g11,g8)
    c: Horizontal(g8)
    c: Horizontal(g10)
    c: Vertical(g9)
    c: Vertical(g11)
    c: Coincident(g8,g3)
    c: Coincident(g9,g7)
    c: Coincident(g4,g8)
    c: Coincident(g5,g10)
    c: PointOnObject(g6,g11)
    c: PointOnObject(g12,g8)
    c: PointOnObject(g13,g10)
    c: Equal(g3,g12)
    c: Equal(g12,g4)
    c: Equal(g7,g13)
    c: Equal(g13,g5)
    c: Equal(g5,g6)
    c: Equal(g6,g0)
    c: Coincident(g14,g6)
    c: Coincident(g14,g4)
    c: Coincident(g15,g7)
    c: Coincident(g6,g15)
    c: Equal(g14,g15)
    c: Coincident(g16,g13)
    c: Coincident(g16,g4)
    c: Coincident(g17,g5)
    c: Coincident(g17,g12)
    c: Coincident(g18,g7)
    c: Equal(g18,g17)
    c: Coincident(g12,g18)
    c: Coincident(g19,g7)
    c: Coincident(g20,g4)
    c: Equal(g20,g19)
    c: Coincident(g21,g5)
    c: Equal(g21,g19)
    c: DistanceY(g0) = 164
    c: Coincident(g22,g3)
    c: Coincident(g22,g13)
    c: Equal(g22,g16)
    c: Coincident(g0,g19)
    c: Coincident(g0,g20)
    c: Coincident(g0,g21)
    c: Coincident(g0,g23)
    c: Coincident(g0,g24)
    c: Equal(g24,g23)
    c: DistanceX(g1,g1) = 336
    c: DistanceX(g2,g2) = 336
    c: Coincident(g23,g2)
    c: Coincident(g24,g2)
    c: Equal(g8,g9)
    c: DistanceX(g8,g8) = 220
FEATURE [PartDesign::Pad] Pad034  label="Bottle-acrylic"
  Length = 4
  Length2 = 100
  Placement = pos=(0,-160.1,36) rot=(0,0.707107,0.707107;3.14159rad)
  Reversed = true
  Sketch = -> Sketch062
  Type = 0
FEATURE [Part::Part2DObjectPython] Rectangle003  label="Acrylic-4mm"  # Draft 2D object (typed FeaturePython)
  ChamferSize = 0
  Columns = 1
  FilletRadius = 0
  Height = 500
  Length = 450
  MakeFace = false
  Placement = pos=(1348.29,1268.18,0) rot=(0,0,1;0rad)
  Rows = 1
FEATURE [Part::Part2DObjectPython] Shape2DView036  label="sBottle-holders"  # Draft 2D object (typed FeaturePython)
  Base = -> Pad034
  HiddenLines = false
  Placement = pos=(1313,1223,0) rot=(0,0,1;0rad)
  Projection = (0,1,5.9605e-08)
  ProjectionMode = 0
  SegmentLength = 0.05
  Tessellation = false
FEATURE [Sketcher::SketchObject] Sketch063
  Placement = pos=(0,-168,0) rot=(-1,0,0;4.71239rad)
  sketch-geometry (4):
    g0: Circle CenterX=98 CenterY=200 CenterZ=0 NormalX=0 NormalY=0 NormalZ=1 Radius=9
    g1: Circle CenterX=103 CenterY=200 CenterZ=0 NormalX=0 NormalY=0 NormalZ=1 Radius=2
    g2: Circle CenterX=93 CenterY=200 CenterZ=0 NormalX=0 NormalY=0 NormalZ=1 Radius=2
    g3: LineSegment [constr] StartX=93 StartY=200 StartZ=0 EndX=103 EndY=200 EndZ=0
  constraints (9):
    c: Radius(g0) = 9
    c: Coincident(g3,g2)
    c: Coincident(g3,g1)
    c: Horizontal(g3)
    c: PointOnObject(g0,g3)
    c: Equal(g1,g2)
    c: Radius(g1) = 2
    c: DistanceX(g3,g3) = 10
    c: DistanceX(g2,g0) = 5
FEATURE [PartDesign::Pad] Pad035  label="Standoff-1"
  Length = 6
  Length2 = 100
  Placement = pos=(0,-168,0) rot=(-1,0,0;4.71239rad)
  Sketch = -> Sketch063
  Type = 0
FEATURE [Part::FeaturePython] Clone006  label="standoff-2"  # Draft clone (typed FeaturePython)
  Objects = -> [Pad035]
  Placement = pos=(54,-168,0) rot=(-1,0,0;4.71239rad)
  Scale = (1,1,1)
FEATURE [Part::Part2DObjectPython] Shape2DView037  label="sBack"  # Draft 2D object (typed FeaturePython)
  Base = -> Draft005
  FaceNumbers = [3]
  HiddenLines = false
  Placement = pos=(1595,660,0) rot=(0,0,1;0rad)
  Projection = (1,0,0)
  ProjectionMode = 0
  SegmentLength = 0.05
  Tessellation = false
FEATURE [Part::Part2DObjectPython] Shape2DView038  label="sStandoff-1"  # Draft 2D object (typed FeaturePython)
  Base = -> Pad035
  HiddenLines = false
  Placement = pos=(240,1240,0) rot=(0,0,1;0rad)
  Projection = (0,-1,5.9605e-08)
  ProjectionMode = 0
  SegmentLength = 0.05
  Tessellation = false
FEATURE [Part::Part2DObjectPython] Clone2D004  label="sStandoff-2"  # Draft 2D object (typed FeaturePython)
  Objects = -> [Shape2DView038]
  Placement = pos=(240,1200,0) rot=(0,0,1;0rad)
  Scale = (1,1,1)
FEATURE [Sketcher::SketchObject] Sketch064
  Placement = pos=(0,167.9,36) rot=(0,0.707107,0.707107;3.14159rad)
  Support = -> Clone005 [Face1]
  sketch-geometry (4):
    g0: LineSegment StartX=-342.171 StartY=279.429 StartZ=0 EndX=-69.188 EndY=279.429 EndZ=0
    g1: LineSegment StartX=-69.188 StartY=279.429 StartZ=0 EndX=-69.188 EndY=45.2128 EndZ=0
    g2: LineSegment StartX=-69.188 StartY=45.2128 StartZ=0 EndX=-342.171 EndY=45.2128 EndZ=0
    g3: LineSegment StartX=-342.171 StartY=45.2128 StartZ=0 EndX=-342.171 EndY=279.429 EndZ=0
  constraints (8):
    c: Coincident(g0,g1)
    c: Coincident(g1,g2)
    c: Coincident(g2,g3)
    c: Coincident(g3,g0)
    c: Horizontal(g0)
    c: Horizontal(g2)
    c: Vertical(g1)
    c: Vertical(g3)
FEATURE [Part::Part2DObjectPython] Shape2DView039  label="sSmall-Gear"  # Draft 2D object (typed FeaturePython)
  Base = -> Pocket007
  FaceNumbers = [4]
  HiddenLines = false
  Placement = pos=(685.446,1501.28,0) rot=(0,0,1;0rad)
  Projection = (0,0,1)
  ProjectionMode = 0
  SegmentLength = 0.05
  Tessellation = false
FEATURE [App::DocumentObjectGroup] Group001  label="Shapes"
  Group = -> [Shape2DView,Shape2DView002,Shape2DView003,Shape2DView006,Shape2DView007,Shape2DView013,Rectangle,Shape2DView010,Shape2DView014,Shape2DView015,Shape2DView016,Shape2DView017,Shape2DView018,Shape2DView019,Shape2DView020,Shape2DView022,Shape2DView023,Shape2DView024,Rectangle001,Shape2DView026,Shape2DView027,Shape2DView028,Shape2DView029,Shape2DView030,Shape2DView031,Shape2DView032,Shape2DView033,+9 more]
